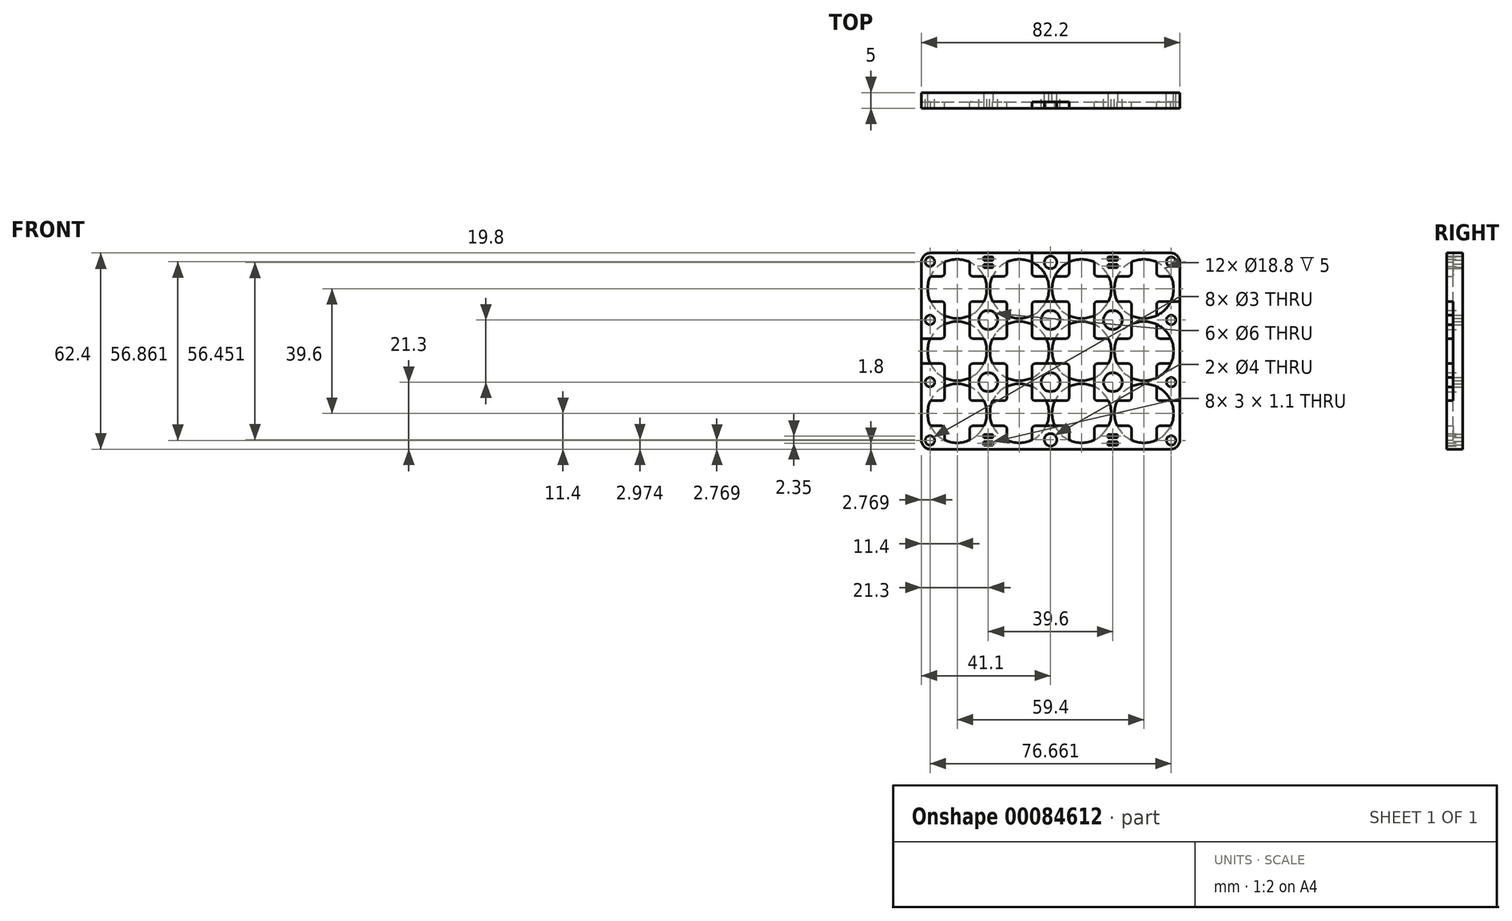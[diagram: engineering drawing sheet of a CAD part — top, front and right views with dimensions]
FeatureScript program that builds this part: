
annotation { "Feature Type Name" : "Feature", "Feature Type Description" : "" }
export const myFeature = defineFeature(function(context is Context, id is Id, definition is map)
    precondition{}
    {
        {
            var Q0;
            Q0=qCreatedBy(makeId("Front.planeOp"),FACE);
            var sketch = newSketch(context, id + "F0", { "sketchPlane" : qUnion([Q0]) });
            skCircle(sketch, "E0", {"center": v(0, 0) * mm, "radius": 9.4 * mm});
            skCircle(sketch, "E1.0.1.0", {"center": v(0, 19.8) * mm, "radius": 9.4 * mm});
            skCircle(sketch, "E1.0.2.0", {"center": v(0, 39.6) * mm, "radius": 9.4 * mm});
            skCircle(sketch, "E1.1.0.0", {"center": v(19.8, 0) * mm, "radius": 9.4 * mm});
            skCircle(sketch, "E1.1.1.0", {"center": v(19.8, 19.8) * mm, "radius": 9.4 * mm});
            skCircle(sketch, "E1.1.2.0", {"center": v(19.8, 39.6) * mm, "radius": 9.4 * mm});
            skCircle(sketch, "E1.2.0.0", {"center": v(39.6, 0) * mm, "radius": 9.4 * mm});
            skCircle(sketch, "E1.2.1.0", {"center": v(39.6, 19.8) * mm, "radius": 9.4 * mm});
            skCircle(sketch, "E1.2.2.0", {"center": v(39.6, 39.6) * mm, "radius": 9.4 * mm});
            skCircle(sketch, "E1.3.0.0", {"center": v(59.4, 0) * mm, "radius": 9.4 * mm});
            skCircle(sketch, "E1.3.1.0", {"center": v(59.4, 19.8) * mm, "radius": 9.4 * mm});
            skCircle(sketch, "E1.3.2.0", {"center": v(59.4, 39.6) * mm, "radius": 9.4 * mm});
            skLineSegment(sketch, "E1.direction1", {"start": v(0, 0) * mm, "end": v(19.8, 0) * mm, "construction": true});
            skLineSegment(sketch, "E1.direction2", {"start": v(0, 0) * mm, "end": v(0, 19.8) * mm, "construction": true});
            skLineSegment(sketch, "E2", {"start": v(-9.4, 19.8) * mm, "end": v(68.8, 19.8) * mm, "construction": true});
            skLineSegment(sketch, "E3", {"start": v(29.7, 19.8) * mm, "end": v(29.7, -16.3) * mm, "construction": true});
            skLineSegment(sketch, "E4.bottom", {"start": v(70.8, -11.4) * mm, "end": v(-11.4, -11.4) * mm});
            skLineSegment(sketch, "E4.top", {"start": v(70.8, 51) * mm, "end": v(-11.4, 51) * mm});
            skLineSegment(sketch, "E4.left", {"start": v(70.8, -11.4) * mm, "end": v(70.8, 51) * mm});
            skLineSegment(sketch, "E4.right", {"start": v(-11.4, -11.4) * mm, "end": v(-11.4, 51) * mm});
            skPoint(sketch, "E4.middle", {"position": v(29.7, 19.8) * mm});
            skLineSegment(sketch, "E5", {"start": v(19.8, 19.8) * mm, "end": v(0, 0) * mm, "construction": true});
            skLineSegment(sketch, "E6", {"start": v(19.8, 0) * mm, "end": v(0, 19.8) * mm, "construction": true});
            skCircle(sketch, "E7", {"center": v(9.9, 9.9) * mm, "radius": 3 * mm});
            skCircle(sketch, "E8.0.1.0", {"center": v(9.9, 29.7) * mm, "radius": 3 * mm});
            skCircle(sketch, "E8.1.0.0", {"center": v(29.7, 9.9) * mm, "radius": 3 * mm});
            skCircle(sketch, "E8.1.1.0", {"center": v(29.7, 29.7) * mm, "radius": 3 * mm});
            skCircle(sketch, "E8.2.0.0", {"center": v(49.5, 9.9) * mm, "radius": 3 * mm});
            skCircle(sketch, "E8.2.1.0", {"center": v(49.5, 29.7) * mm, "radius": 3 * mm});
            skLineSegment(sketch, "E8.direction1", {"start": v(9.9, 9.9) * mm, "end": v(29.7, 9.9) * mm, "construction": true});
            skLineSegment(sketch, "E8.direction2", {"start": v(9.9, 9.9) * mm, "end": v(9.9, 29.7) * mm, "construction": true});
            skLineSegment(sketch, "E9", {"start": v(9.9, 0) * mm, "end": v(9.9, -11.4) * mm, "construction": true});
            skCircle(sketch, "E10.1.0.0", {"center": v(29.7, -8.43) * mm, "radius": 2 * mm});
            skLineSegment(sketch, "E10.direction1", {"start": v(9.9, -8.43) * mm, "end": v(29.7, -8.43) * mm, "construction": true});
            skCircle(sketch, "E11.MirrorC", {"center": v(29.7, 48.03) * mm, "radius": 2 * mm});
            skLineSegment(sketch, "E12", {"start": v(0, 0) * mm, "end": v(-11.4, -11.4) * mm, "construction": true});
            skCircle(sketch, "E13", {"center": v(-8.63, -8.63) * mm, "radius": 1.5 * mm});
            skCircle(sketch, "E14", {"center": v(-8.63, 9.9) * mm, "radius": 1.5 * mm});
            skCircle(sketch, "E15", {"center": v(-8.63, 29.7) * mm, "radius": 1.5 * mm});
            skCircle(sketch, "E16.MirrorC", {"center": v(-8.63, 48.23) * mm, "radius": 1.5 * mm});
            skCircle(sketch, "E17.MirrorC", {"center": v(68.03, -8.63) * mm, "radius": 1.5 * mm});
            skCircle(sketch, "E18.MirrorC", {"center": v(68.03, 9.9) * mm, "radius": 1.5 * mm});
            skCircle(sketch, "E19.MirrorC", {"center": v(68.03, 29.7) * mm, "radius": 1.5 * mm});
            skCircle(sketch, "E20.MirrorC", {"center": v(68.03, 48.23) * mm, "radius": 1.5 * mm});
            skSolve(sketch);
        }
        {
            var Q0;
            Q0=qSketchRegion(id+"F0",true);
            extrude(context, id + "F1", {"entities" : qUnion([Q0]), "depth" : 3 * mm});
        }
        {
            var Q0;
            Q0=makeQuery(id+"F1.opExtrude","SWEPT_EDGE",EDGE,{"disambiguationData":[OSD([sQuery(id+"F0.wireOp",EDGE,"E4.top"),sQuery(id+"F0.wireOp",EDGE,"E4.left")])]});
            var Q1;
            Q1=makeQuery(id+"F1.opExtrude","SWEPT_EDGE",EDGE,{"disambiguationData":[OSD([sQuery(id+"F0.wireOp",EDGE,"E4.top"),sQuery(id+"F0.wireOp",EDGE,"E4.right")])]});
            var Q2;
            Q2=makeQuery(id+"F1.opExtrude","SWEPT_EDGE",EDGE,{"disambiguationData":[OSD([sQuery(id+"F0.wireOp",EDGE,"E4.bottom"),sQuery(id+"F0.wireOp",EDGE,"E4.right")])]});
            var Q3;
            Q3=makeQuery(id+"F1.opExtrude","SWEPT_EDGE",EDGE,{"disambiguationData":[OSD([sQuery(id+"F0.wireOp",EDGE,"E4.bottom"),sQuery(id+"F0.wireOp",EDGE,"E4.left")])]});
            fillet(context, id + "F2", {"entities" : qUnion([Q0, Q1, Q2, Q3]), "radius" : 3 * mm, "tangentPropagation" : true, "conicFillet" : false});
        }
        {
            var Q0;
            Q0=makeQuery(id+"F1.opExtrude","CAP_FACE",FACE,{"disambiguationData":[OSD([sQuery(id+"F0.wireOp",EDGE,"E0"),sQuery(id+"F0.wireOp",EDGE,"E1.0.1.0"),sQuery(id+"F0.wireOp",EDGE,"E1.0.2.0"),sQuery(id+"F0.wireOp",EDGE,"E1.1.0.0"),sQuery(id+"F0.wireOp",EDGE,"E1.1.1.0"),sQuery(id+"F0.wireOp",EDGE,"E1.1.2.0"),sQuery(id+"F0.wireOp",EDGE,"E1.2.0.0"),sQuery(id+"F0.wireOp",EDGE,"E1.2.1.0"),sQuery(id+"F0.wireOp",EDGE,"E1.2.2.0"),sQuery(id+"F0.wireOp",EDGE,"E1.3.0.0"),sQuery(id+"F0.wireOp",EDGE,"E1.3.1.0"),sQuery(id+"F0.wireOp",EDGE,"E1.3.2.0"),sQuery(id+"F0.wireOp",EDGE,"E4.bottom"),sQuery(id+"F0.wireOp",EDGE,"E4.top"),sQuery(id+"F0.wireOp",EDGE,"E4.left"),sQuery(id+"F0.wireOp",EDGE,"E4.right"),sQuery(id+"F0.wireOp",EDGE,"E7"),sQuery(id+"F0.wireOp",EDGE,"E8.0.1.0"),sQuery(id+"F0.wireOp",EDGE,"E8.1.0.0"),sQuery(id+"F0.wireOp",EDGE,"E8.1.1.0"),sQuery(id+"F0.wireOp",EDGE,"E8.2.0.0"),sQuery(id+"F0.wireOp",EDGE,"E8.2.1.0"),sQuery(id+"F0.wireOp",EDGE,"EQu0VpH5-7skk-RFPN-a941-U7lPeWaJFOTF"),sQuery(id+"F0.wireOp",EDGE,"E10.1.0.0"),sQuery(id+"F0.wireOp",EDGE,"E10.2.0.0"),sQuery(id+"F0.wireOp",EDGE,"d1583e0b-7ce3-4cbd-bf89-e67b3cb1275a0.MirrorC"),sQuery(id+"F0.wireOp",EDGE,"E11.MirrorC"),sQuery(id+"F0.wireOp",EDGE,"091dc890-a7a3-4dd7-b955-14caaaf945470.MirrorC"),sQuery(id+"F0.wireOp",EDGE,"E13"),sQuery(id+"F0.wireOp",EDGE,"E14"),sQuery(id+"F0.wireOp",EDGE,"E15"),sQuery(id+"F0.wireOp",EDGE,"E16.MirrorC"),sQuery(id+"F0.wireOp",EDGE,"E17.MirrorC"),sQuery(id+"F0.wireOp",EDGE,"E18.MirrorC"),sQuery(id+"F0.wireOp",EDGE,"E19.MirrorC"),sQuery(id+"F0.wireOp",EDGE,"E20.MirrorC")])],"isStart":false});
            var sketch = newSketch(context, id + "F3", { "sketchPlane" : qUnion([Q0]) });
            skLineSegment(sketch, "E21.0", {"start": v(67.8, 51) * mm, "end": v(-8.4, 51) * mm});
            skArc(sketch, "E21.1", {"start": v(-8.4, 51) * mm, "mid": v(-10.52, 50.12) * mm, "end": v(-11.4, 48) * mm});
            skLineSegment(sketch, "E21.2", {"start": v(-11.4, -8.4) * mm, "end": v(-11.4, 35.6) * mm});
            skArc(sketch, "E21.3", {"start": v(-11.4, -8.4) * mm, "mid": v(-10.52, -10.52) * mm, "end": v(-8.4, -11.4) * mm});
            skLineSegment(sketch, "E21.4", {"start": v(67.8, -11.4) * mm, "end": v(-8.4, -11.4) * mm});
            skArc(sketch, "E21.5", {"start": v(67.8, -11.4) * mm, "mid": v(69.92, -10.52) * mm, "end": v(70.8, -8.4) * mm});
            skLineSegment(sketch, "E21.6", {"start": v(70.8, -8.4) * mm, "end": v(70.8, 48) * mm});
            skArc(sketch, "E21.7", {"start": v(70.8, 48) * mm, "mid": v(69.92, 50.12) * mm, "end": v(67.8, 51) * mm});
            skCircle(sketch, "E21.8", {"center": v(59.4, 39.6) * mm, "radius": 9.4 * mm});
            skCircle(sketch, "E21.9", {"center": v(39.6, 39.6) * mm, "radius": 9.4 * mm});
            skCircle(sketch, "E21.10", {"center": v(19.8, 39.6) * mm, "radius": 9.4 * mm});
            skArc(sketch, "E21.11", {"start": v(-8.5, 43.6) * mm, "mid": v(-9.4, 39.6) * mm, "end": v(-8.5, 35.6) * mm});
            skCircle(sketch, "E21.12", {"center": v(0, 19.8) * mm, "radius": 9.4 * mm});
            skCircle(sketch, "E21.13", {"center": v(19.8, 19.8) * mm, "radius": 9.4 * mm});
            skCircle(sketch, "E21.14", {"center": v(39.6, 19.8) * mm, "radius": 9.4 * mm});
            skCircle(sketch, "E21.15", {"center": v(59.4, 19.8) * mm, "radius": 9.4 * mm});
            skCircle(sketch, "E21.16", {"center": v(59.4, 0) * mm, "radius": 9.4 * mm});
            skCircle(sketch, "E21.17", {"center": v(39.6, 0) * mm, "radius": 9.4 * mm});
            skCircle(sketch, "E21.18", {"center": v(19.8, 0) * mm, "radius": 9.4 * mm});
            skCircle(sketch, "E21.19", {"center": v(0, 0) * mm, "radius": 9.4 * mm});
            skLineSegment(sketch, "E22.left", {"start": v(-11.4, 39.6) * mm, "end": v(-11.4, 43.6) * mm});
            skLineSegment(sketch, "E22.right", {"start": v(70.8, 39.6) * mm, "end": v(70.8, 43.6) * mm});
            skLineSegment(sketch, "E23.trimOffspring", {"start": v(-11.4, 43.6) * mm, "end": v(-11.4, 48) * mm});
            skLineSegment(sketch, "E24", {"start": v(-4, 51) * mm, "end": v(-4, 43.6) * mm});
            skLineSegment(sketch, "E25.MirrorCS", {"start": v(4, 51) * mm, "end": v(4, 43.6) * mm});
            skLineSegment(sketch, "E26", {"start": v(-11.4, -4) * mm, "end": v(-4, -4) * mm});
            skLineSegment(sketch, "E27.MirrorCS", {"start": v(-11.4, 4) * mm, "end": v(-4, 4) * mm});
            skLineSegment(sketch, "E28.1.0.0", {"start": v(15.8, 51) * mm, "end": v(15.8, 43.6) * mm});
            skLineSegment(sketch, "E28.1.0.1", {"start": v(23.8, 51) * mm, "end": v(23.8, 43.6) * mm});
            skLineSegment(sketch, "E28.2.0.0", {"start": v(35.6, 51) * mm, "end": v(35.6, 43.6) * mm});
            skLineSegment(sketch, "E28.2.0.1", {"start": v(43.6, 51) * mm, "end": v(43.6, 43.6) * mm});
            skLineSegment(sketch, "E28.3.0.0", {"start": v(55.4, 51) * mm, "end": v(55.4, 43.6) * mm});
            skLineSegment(sketch, "E28.3.0.1", {"start": v(63.4, 51) * mm, "end": v(63.4, 43.6) * mm});
            skLineSegment(sketch, "E28.direction1", {"start": v(-4, -11.4) * mm, "end": v(15.8, -11.4) * mm, "construction": true});
            skLineSegment(sketch, "E29.0.1.0", {"start": v(-11.4, 23.8) * mm, "end": v(-4, 23.8) * mm});
            skLineSegment(sketch, "E29.0.1.1", {"start": v(-11.4, 15.8) * mm, "end": v(-4, 15.8) * mm});
            skLineSegment(sketch, "E29.0.2.0", {"start": v(-11.4, 43.6) * mm, "end": v(-4, 43.6) * mm});
            skLineSegment(sketch, "E29.0.2.1", {"start": v(-11.4, 35.6) * mm, "end": v(-4, 35.6) * mm});
            skLineSegment(sketch, "E29.direction1", {"start": v(-11.4, 4) * mm, "end": v(-4, 4) * mm, "construction": true});
            skLineSegment(sketch, "E29.direction2", {"start": v(-11.4, 4) * mm, "end": v(-11.4, 23.8) * mm, "construction": true});
            skLineSegment(sketch, "E30.trimOffspring", {"start": v(4, 35.6) * mm, "end": v(15.8, 35.6) * mm});
            skLineSegment(sketch, "E31.trimOffspring", {"start": v(4, 43.6) * mm, "end": v(15.8, 43.6) * mm});
            skLineSegment(sketch, "E32.trimOffspring", {"start": v(4, 35.6) * mm, "end": v(4, 23.8) * mm});
            skLineSegment(sketch, "E33.trimOffspring", {"start": v(-4, 35.6) * mm, "end": v(-4, 23.8) * mm});
            skLineSegment(sketch, "E34.trimOffspring", {"start": v(15.8, 35.6) * mm, "end": v(15.8, 23.8) * mm});
            skLineSegment(sketch, "E35.trimOffspring", {"start": v(23.8, 35.6) * mm, "end": v(23.8, 23.8) * mm});
            skLineSegment(sketch, "E36.trimOffspring", {"start": v(35.6, 35.6) * mm, "end": v(35.6, 23.8) * mm});
            skLineSegment(sketch, "E37.trimOffspring", {"start": v(43.6, 35.6) * mm, "end": v(43.6, 23.8) * mm});
            skLineSegment(sketch, "E38.trimOffspring", {"start": v(55.4, 35.6) * mm, "end": v(55.4, 23.8) * mm});
            skLineSegment(sketch, "E39.trimOffspring", {"start": v(63.4, 35.6) * mm, "end": v(63.4, 23.8) * mm});
            skLineSegment(sketch, "E40.trimOffspring", {"start": v(23.8, 43.6) * mm, "end": v(35.6, 43.6) * mm});
            skLineSegment(sketch, "E41.trimOffspring", {"start": v(43.6, 43.6) * mm, "end": v(55.4, 43.6) * mm});
            skLineSegment(sketch, "E42.trimOffspring", {"start": v(63.4, 43.6) * mm, "end": v(70.8, 43.6) * mm});
            skLineSegment(sketch, "E43.trimOffspring", {"start": v(63.4, 35.6) * mm, "end": v(70.8, 35.6) * mm});
            skLineSegment(sketch, "E44.trimOffspring", {"start": v(43.6, 35.6) * mm, "end": v(55.4, 35.6) * mm});
            skLineSegment(sketch, "E45.trimOffspring", {"start": v(23.8, 35.6) * mm, "end": v(35.6, 35.6) * mm});
            skLineSegment(sketch, "E46.trimOffspring", {"start": v(4, 23.8) * mm, "end": v(15.8, 23.8) * mm});
            skLineSegment(sketch, "E47.trimOffspring", {"start": v(4, 15.8) * mm, "end": v(11.3, 15.8) * mm});
            skLineSegment(sketch, "E48.trimOffspring", {"start": v(-4, 15.8) * mm, "end": v(-4, 4) * mm});
            skLineSegment(sketch, "E49.trimOffspring", {"start": v(4, 15.8) * mm, "end": v(4, 4) * mm});
            skLineSegment(sketch, "E50.trimOffspring", {"start": v(15.8, 15.8) * mm, "end": v(15.8, 4) * mm});
            skLineSegment(sketch, "E51.trimOffspring", {"start": v(23.8, 15.8) * mm, "end": v(23.8, 4) * mm});
            skLineSegment(sketch, "E52.trimOffspring", {"start": v(35.6, 15.8) * mm, "end": v(35.6, 4) * mm});
            skLineSegment(sketch, "E53.trimOffspring", {"start": v(43.6, 15.8) * mm, "end": v(43.6, 4) * mm});
            skLineSegment(sketch, "E54.trimOffspring", {"start": v(55.4, 15.8) * mm, "end": v(55.4, 4) * mm});
            skLineSegment(sketch, "E55.trimOffspring", {"start": v(63.4, 15.8) * mm, "end": v(63.4, 4) * mm});
            skLineSegment(sketch, "E56.trimOffspring", {"start": v(23.8, 23.8) * mm, "end": v(35.6, 23.8) * mm});
            skLineSegment(sketch, "E57.trimOffspring", {"start": v(43.6, 23.8) * mm, "end": v(55.4, 23.8) * mm});
            skLineSegment(sketch, "E58.trimOffspring", {"start": v(63.4, 23.8) * mm, "end": v(70.8, 23.8) * mm});
            skLineSegment(sketch, "E59.trimOffspring", {"start": v(23.8, 15.8) * mm, "end": v(35.6, 15.8) * mm});
            skLineSegment(sketch, "E60.trimOffspring", {"start": v(63.4, 15.8) * mm, "end": v(70.8, 15.8) * mm});
            skLineSegment(sketch, "E61.trimOffspring", {"start": v(63.4, 4) * mm, "end": v(70.8, 4) * mm});
            skLineSegment(sketch, "E62.trimOffspring", {"start": v(43.6, 4) * mm, "end": v(55.4, 4) * mm});
            skLineSegment(sketch, "E63.trimOffspring", {"start": v(23.8, 4) * mm, "end": v(35.6, 4) * mm});
            skLineSegment(sketch, "E64.trimOffspring", {"start": v(4, 4) * mm, "end": v(15.8, 4) * mm});
            skLineSegment(sketch, "E65.trimOffspring", {"start": v(4, -4) * mm, "end": v(11.3, -4) * mm});
            skLineSegment(sketch, "E66.trimOffspring", {"start": v(23.8, -4) * mm, "end": v(35.6, -4) * mm});
            skLineSegment(sketch, "E67.trimOffspring", {"start": v(63.4, -4) * mm, "end": v(70.8, -4) * mm});
            skLineSegment(sketch, "E68.trimOffspring", {"start": v(55.4, -4) * mm, "end": v(55.4, -11.4) * mm});
            skLineSegment(sketch, "E69.trimOffspring", {"start": v(63.4, -4) * mm, "end": v(63.4, -11.4) * mm});
            skLineSegment(sketch, "E70.trimOffspring", {"start": v(43.6, -4) * mm, "end": v(43.6, -11.4) * mm});
            skLineSegment(sketch, "E71.trimOffspring", {"start": v(35.6, -4) * mm, "end": v(35.6, -11.4) * mm});
            skLineSegment(sketch, "E72.trimOffspring", {"start": v(23.8, -4) * mm, "end": v(23.8, -11.4) * mm});
            skLineSegment(sketch, "E73.trimOffspring", {"start": v(4, -4) * mm, "end": v(4, -11.4) * mm});
            skLineSegment(sketch, "E74.trimOffspring", {"start": v(-4, -4) * mm, "end": v(-4, -11.4) * mm});
            skLineSegment(sketch, "E75", {"start": v(11.3, 15.8) * mm, "end": v(15.8, 15.8) * mm});
            skLineSegment(sketch, "E76", {"start": v(11.3, -4) * mm, "end": v(15.8, -4) * mm});
            skLineSegment(sketch, "E77.trimOffspring", {"start": v(15.8, -4) * mm, "end": v(15.8, -11.4) * mm});
            skLineSegment(sketch, "E78.trimOffspring", {"start": v(43.6, 15.8) * mm, "end": v(55.4, 15.8) * mm});
            skLineSegment(sketch, "E79.trimOffspring", {"start": v(4, 4) * mm, "end": v(13.6, 4) * mm, "construction": true});
            skLineSegment(sketch, "E80.trimOffspring", {"start": v(43.6, -4) * mm, "end": v(55.4, -4) * mm});
            skArc(sketch, "E81.trimOffspring", {"start": v(4, 48.1) * mm, "mid": v(0, 49) * mm, "end": v(-4, 48.1) * mm});
            skArc(sketch, "E82.trimOffspring", {"start": v(8.5, 35.6) * mm, "mid": v(9.4, 39.6) * mm, "end": v(8.5, 43.6) * mm});
            skArc(sketch, "E83.trimOffspring", {"start": v(-4, 31.1) * mm, "mid": v(0, 30.2) * mm, "end": v(4, 31.1) * mm});
            skSolve(sketch);
        }
        {
            var Q0;
            {var subQ6=sQuery(id+"F3.wireOp",EDGE,"E21.1");Q0=makeQuery(id+"F3.imprint","IMPRINT",FACE,{"disambiguationData":[TD([[makeQuery(id+"F3.imprint","IMPRINT",EDGE,{"derivedFrom":subQ6}),1.0]])]});}
            var Q1;
            {var subQ0=sQuery(id+"F3.wireOp",EDGE,"E29.0.2.0");var subQ1=sQuery(id+"F3.wireOp",EDGE,"E24");var subQ2=makeQuery(id+"F3.imprint","INTERSECT",VERTEX,{"derivedFrom":[subQ1,subQ0]});Q1=makeQuery(id+"F3.imprint","IMPRINT",FACE,{"disambiguationData":[TD([[makeQuery(id+"F3.imprint","IMPRINT",EDGE,{"disambiguationData":[TD([[subQ2,1.0]])],"derivedFrom":subQ1}),-1.0]])]});}
            var Q2;
            {var subQ0=sQuery(id+"F3.wireOp",EDGE,"E31.trimOffspring");var subQ1=sQuery(id+"F3.wireOp",EDGE,"E25.MirrorCS");var subQ2=makeQuery(id+"F3.imprint","INTERSECT",VERTEX,{"derivedFrom":[subQ1,subQ0]});Q2=makeQuery(id+"F3.imprint","IMPRINT",FACE,{"disambiguationData":[TD([[makeQuery(id+"F3.imprint","IMPRINT",EDGE,{"disambiguationData":[TD([[subQ2,1.0]])],"derivedFrom":subQ1}),1.0]])]});}
            var Q3;
            Q3=makeQuery(id+"F3.imprint","IMPRINT",FACE,{"disambiguationData":[TD([[makeQuery(id+"F3.imprint","IMPRINT",EDGE,{"derivedFrom":makeQuery(id+"F1.opExtrude","CAP_EDGE",EDGE,{"disambiguationData":[OSD([sQuery(id+"F0.wireOp",EDGE,"d1583e0b-7ce3-4cbd-bf89-e67b3cb1275a0.MirrorC")])],"isStart":false})}),1.0]])]});
            var Q4;
            {var subQ0=sQuery(id+"F3.wireOp",EDGE,"E31.trimOffspring");var subQ1=sQuery(id+"F3.wireOp",EDGE,"E28.1.0.0");var subQ2=makeQuery(id+"F3.imprint","INTERSECT",VERTEX,{"derivedFrom":[subQ1,subQ0]});Q4=makeQuery(id+"F3.imprint","IMPRINT",FACE,{"disambiguationData":[TD([[makeQuery(id+"F3.imprint","IMPRINT",EDGE,{"disambiguationData":[TD([[subQ2,1.0]])],"derivedFrom":subQ1}),-1.0]])]});}
            var Q5;
            {var subQ0=sQuery(id+"F3.wireOp",EDGE,"E40.trimOffspring");var subQ1=sQuery(id+"F3.wireOp",EDGE,"E28.1.0.1");var subQ2=makeQuery(id+"F3.imprint","INTERSECT",VERTEX,{"derivedFrom":[subQ1,subQ0]});Q5=makeQuery(id+"F3.imprint","IMPRINT",FACE,{"disambiguationData":[TD([[makeQuery(id+"F3.imprint","IMPRINT",EDGE,{"disambiguationData":[TD([[subQ2,1.0]])],"derivedFrom":subQ1}),1.0]])]});}
            var Q6;
            Q6=makeQuery(id+"F3.imprint","IMPRINT",FACE,{"disambiguationData":[TD([[makeQuery(id+"F3.imprint","IMPRINT",EDGE,{"derivedFrom":makeQuery(id+"F1.opExtrude","CAP_EDGE",EDGE,{"disambiguationData":[OSD([sQuery(id+"F0.wireOp",EDGE,"E11.MirrorC")])],"isStart":false})}),1.0]])]});
            var Q7;
            {var subQ0=sQuery(id+"F3.wireOp",EDGE,"E28.2.0.0");var subQ1=sQuery(id+"F3.wireOp",EDGE,"E21.9");var subQ2=makeQuery(id+"F3.imprint","INTERSECT",VERTEX,{"derivedFrom":[subQ1,subQ0]});Q7=makeQuery(id+"F3.imprint","IMPRINT",FACE,{"disambiguationData":[TD([[makeQuery(id+"F3.imprint","IMPRINT",EDGE,{"disambiguationData":[TD([[subQ2,-1.0]])],"derivedFrom":subQ1}),1.0]])]});}
            var Q8;
            {var subQ0=sQuery(id+"F3.wireOp",EDGE,"E28.2.0.1");var subQ1=sQuery(id+"F3.wireOp",EDGE,"E21.9");var subQ2=makeQuery(id+"F3.imprint","INTERSECT",VERTEX,{"derivedFrom":[subQ1,subQ0]});Q8=makeQuery(id+"F3.imprint","IMPRINT",FACE,{"disambiguationData":[TD([[makeQuery(id+"F3.imprint","IMPRINT",EDGE,{"disambiguationData":[TD([[subQ2,1.0]])],"derivedFrom":subQ1}),1.0]])]});}
            var Q9;
            Q9=makeQuery(id+"F3.imprint","IMPRINT",FACE,{"disambiguationData":[TD([[makeQuery(id+"F3.imprint","IMPRINT",EDGE,{"derivedFrom":makeQuery(id+"F1.opExtrude","CAP_EDGE",EDGE,{"disambiguationData":[OSD([sQuery(id+"F0.wireOp",EDGE,"091dc890-a7a3-4dd7-b955-14caaaf945470.MirrorC")])],"isStart":false})}),1.0]])]});
            var Q10;
            {var subQ0=sQuery(id+"F3.wireOp",EDGE,"E41.trimOffspring");var subQ1=sQuery(id+"F3.wireOp",EDGE,"E28.3.0.0");var subQ2=makeQuery(id+"F3.imprint","INTERSECT",VERTEX,{"derivedFrom":[subQ1,subQ0]});Q10=makeQuery(id+"F3.imprint","IMPRINT",FACE,{"disambiguationData":[TD([[makeQuery(id+"F3.imprint","IMPRINT",EDGE,{"disambiguationData":[TD([[subQ2,1.0]])],"derivedFrom":subQ1}),-1.0]])]});}
            var Q11;
            {var subQ0=sQuery(id+"F3.wireOp",EDGE,"E42.trimOffspring");var subQ1=sQuery(id+"F3.wireOp",EDGE,"E28.3.0.1");var subQ2=makeQuery(id+"F3.imprint","INTERSECT",VERTEX,{"derivedFrom":[subQ1,subQ0]});Q11=makeQuery(id+"F3.imprint","IMPRINT",FACE,{"disambiguationData":[TD([[makeQuery(id+"F3.imprint","IMPRINT",EDGE,{"disambiguationData":[TD([[subQ2,1.0]])],"derivedFrom":subQ1}),1.0]])]});}
            var Q12;
            {var subQ9=sQuery(id+"F3.wireOp",EDGE,"E21.7");Q12=makeQuery(id+"F3.imprint","IMPRINT",FACE,{"disambiguationData":[TD([[makeQuery(id+"F3.imprint","IMPRINT",EDGE,{"derivedFrom":subQ9}),1.0]])]});}
            var Q13;
            {var subQ0=sQuery(id+"F3.wireOp",EDGE,"E58.trimOffspring");var subQ1=sQuery(id+"F3.wireOp",EDGE,"E39.trimOffspring");var subQ2=makeQuery(id+"F3.imprint","INTERSECT",VERTEX,{"derivedFrom":[subQ1,subQ0]});Q13=makeQuery(id+"F3.imprint","IMPRINT",FACE,{"disambiguationData":[TD([[makeQuery(id+"F3.imprint","IMPRINT",EDGE,{"disambiguationData":[TD([[subQ2,1.0]])],"derivedFrom":subQ1}),1.0]])]});}
            var Q14;
            Q14=makeQuery(id+"F3.imprint","IMPRINT",FACE,{"disambiguationData":[TD([[makeQuery(id+"F3.imprint","IMPRINT",EDGE,{"derivedFrom":makeQuery(id+"F1.opExtrude","CAP_EDGE",EDGE,{"disambiguationData":[OSD([sQuery(id+"F0.wireOp",EDGE,"E19.MirrorC")])],"isStart":false})}),1.0]])]});
            var Q15;
            {var subQ0=sQuery(id+"F3.wireOp",EDGE,"E43.trimOffspring");var subQ1=sQuery(id+"F3.wireOp",EDGE,"E39.trimOffspring");var subQ2=makeQuery(id+"F3.imprint","INTERSECT",VERTEX,{"derivedFrom":[subQ1,subQ0]});Q15=makeQuery(id+"F3.imprint","IMPRINT",FACE,{"disambiguationData":[TD([[makeQuery(id+"F3.imprint","IMPRINT",EDGE,{"disambiguationData":[TD([[subQ2,-1.0]])],"derivedFrom":subQ1}),1.0]])]});}
            var Q16;
            {var subQ0=sQuery(id+"F3.wireOp",EDGE,"E57.trimOffspring");var subQ1=sQuery(id+"F3.wireOp",EDGE,"E38.trimOffspring");var subQ2=makeQuery(id+"F3.imprint","INTERSECT",VERTEX,{"derivedFrom":[subQ1,subQ0]});Q16=makeQuery(id+"F3.imprint","IMPRINT",FACE,{"disambiguationData":[TD([[makeQuery(id+"F3.imprint","IMPRINT",EDGE,{"disambiguationData":[TD([[subQ2,1.0]])],"derivedFrom":subQ1}),-1.0]])]});}
            var Q17;
            {var subQ0=sQuery(id+"F3.wireOp",EDGE,"E57.trimOffspring");var subQ1=sQuery(id+"F3.wireOp",EDGE,"E37.trimOffspring");var subQ2=makeQuery(id+"F3.imprint","INTERSECT",VERTEX,{"derivedFrom":[subQ1,subQ0]});Q17=makeQuery(id+"F3.imprint","IMPRINT",FACE,{"disambiguationData":[TD([[makeQuery(id+"F3.imprint","IMPRINT",EDGE,{"disambiguationData":[TD([[subQ2,1.0]])],"derivedFrom":subQ1}),1.0]])]});}
            var Q18;
            {var subQ0=sQuery(id+"F3.wireOp",EDGE,"E37.trimOffspring");var subQ1=sQuery(id+"F3.wireOp",EDGE,"E21.9");var subQ2=makeQuery(id+"F3.imprint","INTERSECT",VERTEX,{"derivedFrom":[subQ1,subQ0]});Q18=makeQuery(id+"F3.imprint","IMPRINT",FACE,{"disambiguationData":[TD([[makeQuery(id+"F3.imprint","IMPRINT",EDGE,{"disambiguationData":[TD([[subQ2,-1.0]])],"derivedFrom":subQ1}),1.0]])]});}
            var Q19;
            {var subQ0=sQuery(id+"F3.wireOp",EDGE,"E44.trimOffspring");var subQ1=sQuery(id+"F3.wireOp",EDGE,"E38.trimOffspring");var subQ2=makeQuery(id+"F3.imprint","INTERSECT",VERTEX,{"derivedFrom":[subQ1,subQ0]});Q19=makeQuery(id+"F3.imprint","IMPRINT",FACE,{"disambiguationData":[TD([[makeQuery(id+"F3.imprint","IMPRINT",EDGE,{"disambiguationData":[TD([[subQ2,-1.0]])],"derivedFrom":subQ1}),-1.0]])]});}
            var Q20;
            Q20=makeQuery(id+"F3.imprint","IMPRINT",FACE,{"disambiguationData":[TD([[makeQuery(id+"F3.imprint","IMPRINT",EDGE,{"derivedFrom":makeQuery(id+"F1.opExtrude","CAP_EDGE",EDGE,{"disambiguationData":[OSD([sQuery(id+"F0.wireOp",EDGE,"E8.2.1.0")])],"isStart":false})}),-1.0]])]});
            var Q21;
            {var subQ0=sQuery(id+"F3.wireOp",EDGE,"E45.trimOffspring");var subQ1=sQuery(id+"F3.wireOp",EDGE,"E35.trimOffspring");var subQ2=makeQuery(id+"F3.imprint","INTERSECT",VERTEX,{"derivedFrom":[subQ1,subQ0]});Q21=makeQuery(id+"F3.imprint","IMPRINT",FACE,{"disambiguationData":[TD([[makeQuery(id+"F3.imprint","IMPRINT",EDGE,{"disambiguationData":[TD([[subQ2,-1.0]])],"derivedFrom":subQ1}),1.0]])]});}
            var Q22;
            {var subQ0=sQuery(id+"F3.wireOp",EDGE,"E56.trimOffspring");var subQ1=sQuery(id+"F3.wireOp",EDGE,"E35.trimOffspring");var subQ2=makeQuery(id+"F3.imprint","INTERSECT",VERTEX,{"derivedFrom":[subQ1,subQ0]});Q22=makeQuery(id+"F3.imprint","IMPRINT",FACE,{"disambiguationData":[TD([[makeQuery(id+"F3.imprint","IMPRINT",EDGE,{"disambiguationData":[TD([[subQ2,1.0]])],"derivedFrom":subQ1}),1.0]])]});}
            var Q23;
            {var subQ0=sQuery(id+"F3.wireOp",EDGE,"E56.trimOffspring");var subQ1=sQuery(id+"F3.wireOp",EDGE,"E36.trimOffspring");var subQ2=makeQuery(id+"F3.imprint","INTERSECT",VERTEX,{"derivedFrom":[subQ1,subQ0]});Q23=makeQuery(id+"F3.imprint","IMPRINT",FACE,{"disambiguationData":[TD([[makeQuery(id+"F3.imprint","IMPRINT",EDGE,{"disambiguationData":[TD([[subQ2,1.0]])],"derivedFrom":subQ1}),-1.0]])]});}
            var Q24;
            {var subQ0=sQuery(id+"F3.wireOp",EDGE,"E45.trimOffspring");var subQ1=sQuery(id+"F3.wireOp",EDGE,"E21.9");var subQ2=makeQuery(id+"F3.imprint","INTERSECT",VERTEX,{"derivedFrom":[subQ1,subQ0]});Q24=makeQuery(id+"F3.imprint","IMPRINT",FACE,{"disambiguationData":[TD([[makeQuery(id+"F3.imprint","IMPRINT",EDGE,{"disambiguationData":[TD([[subQ2,-1.0]])],"derivedFrom":subQ1}),1.0]])]});}
            var Q25;
            Q25=makeQuery(id+"F3.imprint","IMPRINT",FACE,{"disambiguationData":[TD([[makeQuery(id+"F3.imprint","IMPRINT",EDGE,{"derivedFrom":makeQuery(id+"F1.opExtrude","CAP_EDGE",EDGE,{"disambiguationData":[OSD([sQuery(id+"F0.wireOp",EDGE,"E8.1.1.0")])],"isStart":false})}),-1.0]])]});
            var Q26;
            Q26=makeQuery(id+"F3.imprint","IMPRINT",FACE,{"disambiguationData":[TD([[makeQuery(id+"F3.imprint","IMPRINT",EDGE,{"derivedFrom":makeQuery(id+"F1.opExtrude","CAP_EDGE",EDGE,{"disambiguationData":[OSD([sQuery(id+"F0.wireOp",EDGE,"E8.0.1.0")])],"isStart":false})}),-1.0]])]});
            var Q27;
            {var subQ0=sQuery(id+"F3.wireOp",EDGE,"E32.trimOffspring");var subQ1=sQuery(id+"F3.wireOp",EDGE,"E30.trimOffspring");var subQ2=makeQuery(id+"F3.imprint","INTERSECT",VERTEX,{"derivedFrom":[subQ1,subQ0]});Q27=makeQuery(id+"F3.imprint","IMPRINT",FACE,{"disambiguationData":[TD([[makeQuery(id+"F3.imprint","IMPRINT",EDGE,{"disambiguationData":[TD([[subQ2,-1.0]])],"derivedFrom":subQ1}),-1.0]])]});}
            var Q28;
            {var subQ0=sQuery(id+"F3.wireOp",EDGE,"E34.trimOffspring");var subQ1=sQuery(id+"F3.wireOp",EDGE,"E30.trimOffspring");var subQ2=makeQuery(id+"F3.imprint","INTERSECT",VERTEX,{"derivedFrom":[subQ1,subQ0]});Q28=makeQuery(id+"F3.imprint","IMPRINT",FACE,{"disambiguationData":[TD([[makeQuery(id+"F3.imprint","IMPRINT",EDGE,{"disambiguationData":[TD([[subQ2,1.0]])],"derivedFrom":subQ1}),-1.0]])]});}
            var Q29;
            {var subQ0=sQuery(id+"F3.wireOp",EDGE,"E46.trimOffspring");var subQ1=sQuery(id+"F3.wireOp",EDGE,"E34.trimOffspring");var subQ2=makeQuery(id+"F3.imprint","INTERSECT",VERTEX,{"derivedFrom":[subQ1,subQ0]});Q29=makeQuery(id+"F3.imprint","IMPRINT",FACE,{"disambiguationData":[TD([[makeQuery(id+"F3.imprint","IMPRINT",EDGE,{"disambiguationData":[TD([[subQ2,1.0]])],"derivedFrom":subQ1}),-1.0]])]});}
            var Q30;
            {var subQ0=sQuery(id+"F3.wireOp",EDGE,"E46.trimOffspring");var subQ1=sQuery(id+"F3.wireOp",EDGE,"E32.trimOffspring");var subQ2=makeQuery(id+"F3.imprint","INTERSECT",VERTEX,{"derivedFrom":[subQ1,subQ0]});Q30=makeQuery(id+"F3.imprint","IMPRINT",FACE,{"disambiguationData":[TD([[makeQuery(id+"F3.imprint","IMPRINT",EDGE,{"disambiguationData":[TD([[subQ2,1.0]])],"derivedFrom":subQ1}),1.0]])]});}
            var Q31;
            Q31=makeQuery(id+"F3.imprint","IMPRINT",FACE,{"disambiguationData":[TD([[makeQuery(id+"F3.imprint","IMPRINT",EDGE,{"derivedFrom":makeQuery(id+"F1.opExtrude","CAP_EDGE",EDGE,{"disambiguationData":[OSD([sQuery(id+"F0.wireOp",EDGE,"E14")])],"isStart":false})}),-1.0]])]});
            var Q32;
            {var subQ0=sQuery(id+"F3.wireOp",EDGE,"E48.trimOffspring");var subQ1=sQuery(id+"F3.wireOp",EDGE,"E29.0.1.1");var subQ2=makeQuery(id+"F3.imprint","INTERSECT",VERTEX,{"derivedFrom":[subQ1,subQ0]});Q32=makeQuery(id+"F3.imprint","IMPRINT",FACE,{"disambiguationData":[TD([[makeQuery(id+"F3.imprint","IMPRINT",EDGE,{"disambiguationData":[TD([[subQ2,1.0]])],"derivedFrom":subQ1}),-1.0]])]});}
            var Q33;
            {var subQ0=sQuery(id+"F3.wireOp",EDGE,"E48.trimOffspring");var subQ1=sQuery(id+"F3.wireOp",EDGE,"E27.MirrorCS");var subQ2=makeQuery(id+"F3.imprint","INTERSECT",VERTEX,{"derivedFrom":[subQ1,subQ0]});Q33=makeQuery(id+"F3.imprint","IMPRINT",FACE,{"disambiguationData":[TD([[makeQuery(id+"F3.imprint","IMPRINT",EDGE,{"disambiguationData":[TD([[subQ2,1.0]])],"derivedFrom":subQ1}),1.0]])]});}
            var Q34;
            {var subQ1=sQuery(id+"F3.wireOp",EDGE,"E21.3");Q34=makeQuery(id+"F3.imprint","IMPRINT",FACE,{"disambiguationData":[TD([[makeQuery(id+"F3.imprint","IMPRINT",EDGE,{"derivedFrom":subQ1}),1.0]])]});}
            var Q35;
            {var subQ0=sQuery(id+"F3.wireOp",EDGE,"E74.trimOffspring");var subQ1=sQuery(id+"F3.wireOp",EDGE,"E26");var subQ2=makeQuery(id+"F3.imprint","INTERSECT",VERTEX,{"derivedFrom":[subQ1,subQ0]});Q35=makeQuery(id+"F3.imprint","IMPRINT",FACE,{"disambiguationData":[TD([[makeQuery(id+"F3.imprint","IMPRINT",EDGE,{"disambiguationData":[TD([[subQ2,1.0]])],"derivedFrom":subQ1}),-1.0]])]});}
            var Q36;
            Q36=makeQuery(id+"F3.imprint","IMPRINT",FACE,{"disambiguationData":[TD([[makeQuery(id+"F3.imprint","IMPRINT",EDGE,{"derivedFrom":makeQuery(id+"F1.opExtrude","CAP_EDGE",EDGE,{"disambiguationData":[OSD([sQuery(id+"F0.wireOp",EDGE,"EQu0VpH5-7skk-RFPN-a941-U7lPeWaJFOTF")])],"isStart":false})}),-1.0]])]});
            var Q37;
            {var subQ0=sQuery(id+"F3.wireOp",EDGE,"E73.trimOffspring");var subQ1=sQuery(id+"F3.wireOp",EDGE,"E65.trimOffspring");var subQ2=makeQuery(id+"F3.imprint","INTERSECT",VERTEX,{"derivedFrom":[subQ1,subQ0]});Q37=makeQuery(id+"F3.imprint","IMPRINT",FACE,{"disambiguationData":[TD([[makeQuery(id+"F3.imprint","IMPRINT",EDGE,{"disambiguationData":[TD([[subQ2,-1.0]])],"derivedFrom":subQ1}),-1.0]])]});}
            var Q38;
            {var subQ0=sQuery(id+"F3.wireOp",EDGE,"E76");Q38=makeQuery(id+"F3.imprint","IMPRINT",FACE,{"disambiguationData":[TD([[makeQuery(id+"F3.imprint","IMPRINT",EDGE,{"derivedFrom":subQ0}),-1.0]])]});}
            var Q39;
            Q39=makeQuery(id+"F3.imprint","IMPRINT",FACE,{"disambiguationData":[TD([[makeQuery(id+"F3.imprint","IMPRINT",EDGE,{"derivedFrom":makeQuery(id+"F1.opExtrude","CAP_EDGE",EDGE,{"disambiguationData":[OSD([sQuery(id+"F0.wireOp",EDGE,"E10.1.0.0")])],"isStart":false})}),-1.0]])]});
            var Q40;
            {var subQ0=sQuery(id+"F3.wireOp",EDGE,"E72.trimOffspring");var subQ1=sQuery(id+"F3.wireOp",EDGE,"E66.trimOffspring");var subQ2=makeQuery(id+"F3.imprint","INTERSECT",VERTEX,{"derivedFrom":[subQ1,subQ0]});Q40=makeQuery(id+"F3.imprint","IMPRINT",FACE,{"disambiguationData":[TD([[makeQuery(id+"F3.imprint","IMPRINT",EDGE,{"disambiguationData":[TD([[subQ2,-1.0]])],"derivedFrom":subQ1}),-1.0]])]});}
            var Q41;
            {var subQ0=sQuery(id+"F3.wireOp",EDGE,"E71.trimOffspring");var subQ1=sQuery(id+"F3.wireOp",EDGE,"E66.trimOffspring");var subQ2=makeQuery(id+"F3.imprint","INTERSECT",VERTEX,{"derivedFrom":[subQ1,subQ0]});Q41=makeQuery(id+"F3.imprint","IMPRINT",FACE,{"disambiguationData":[TD([[makeQuery(id+"F3.imprint","IMPRINT",EDGE,{"disambiguationData":[TD([[subQ2,1.0]])],"derivedFrom":subQ1}),-1.0]])]});}
            var Q42;
            Q42=makeQuery(id+"F3.imprint","IMPRINT",FACE,{"disambiguationData":[TD([[makeQuery(id+"F3.imprint","IMPRINT",EDGE,{"derivedFrom":makeQuery(id+"F1.opExtrude","CAP_EDGE",EDGE,{"disambiguationData":[OSD([sQuery(id+"F0.wireOp",EDGE,"E10.2.0.0")])],"isStart":false})}),-1.0]])]});
            var Q43;
            {var subQ0=sQuery(id+"F3.wireOp",EDGE,"E80.trimOffspring");var subQ1=sQuery(id+"F3.wireOp",EDGE,"E70.trimOffspring");var subQ2=makeQuery(id+"F3.imprint","INTERSECT",VERTEX,{"derivedFrom":[subQ1,subQ0]});Q43=makeQuery(id+"F3.imprint","IMPRINT",FACE,{"disambiguationData":[TD([[makeQuery(id+"F3.imprint","IMPRINT",EDGE,{"disambiguationData":[TD([[subQ2,-1.0]])],"derivedFrom":subQ1}),1.0]])]});}
            var Q44;
            {var subQ0=sQuery(id+"F3.wireOp",EDGE,"E80.trimOffspring");var subQ1=sQuery(id+"F3.wireOp",EDGE,"E68.trimOffspring");var subQ2=makeQuery(id+"F3.imprint","INTERSECT",VERTEX,{"derivedFrom":[subQ1,subQ0]});Q44=makeQuery(id+"F3.imprint","IMPRINT",FACE,{"disambiguationData":[TD([[makeQuery(id+"F3.imprint","IMPRINT",EDGE,{"disambiguationData":[TD([[subQ2,-1.0]])],"derivedFrom":subQ1}),-1.0]])]});}
            var Q45;
            {var subQ0=sQuery(id+"F3.wireOp",EDGE,"E69.trimOffspring");var subQ1=sQuery(id+"F3.wireOp",EDGE,"E67.trimOffspring");var subQ2=makeQuery(id+"F3.imprint","INTERSECT",VERTEX,{"derivedFrom":[subQ1,subQ0]});Q45=makeQuery(id+"F3.imprint","IMPRINT",FACE,{"disambiguationData":[TD([[makeQuery(id+"F3.imprint","IMPRINT",EDGE,{"disambiguationData":[TD([[subQ2,-1.0]])],"derivedFrom":subQ1}),-1.0]])]});}
            var Q46;
            {var subQ1=sQuery(id+"F3.wireOp",EDGE,"E21.5");Q46=makeQuery(id+"F3.imprint","IMPRINT",FACE,{"disambiguationData":[TD([[makeQuery(id+"F3.imprint","IMPRINT",EDGE,{"derivedFrom":subQ1}),1.0]])]});}
            var Q47;
            Q47=makeQuery(id+"F3.imprint","IMPRINT",FACE,{"disambiguationData":[TD([[makeQuery(id+"F3.imprint","IMPRINT",EDGE,{"derivedFrom":makeQuery(id+"F1.opExtrude","CAP_EDGE",EDGE,{"disambiguationData":[OSD([sQuery(id+"F0.wireOp",EDGE,"E18.MirrorC")])],"isStart":false})}),1.0]])]});
            var Q48;
            {var subQ0=sQuery(id+"F3.wireOp",EDGE,"E61.trimOffspring");var subQ1=sQuery(id+"F3.wireOp",EDGE,"E55.trimOffspring");var subQ2=makeQuery(id+"F3.imprint","INTERSECT",VERTEX,{"derivedFrom":[subQ1,subQ0]});Q48=makeQuery(id+"F3.imprint","IMPRINT",FACE,{"disambiguationData":[TD([[makeQuery(id+"F3.imprint","IMPRINT",EDGE,{"disambiguationData":[TD([[subQ2,1.0]])],"derivedFrom":subQ1}),1.0]])]});}
            var Q49;
            {var subQ0=sQuery(id+"F3.wireOp",EDGE,"E60.trimOffspring");var subQ1=sQuery(id+"F3.wireOp",EDGE,"E55.trimOffspring");var subQ2=makeQuery(id+"F3.imprint","INTERSECT",VERTEX,{"derivedFrom":[subQ1,subQ0]});Q49=makeQuery(id+"F3.imprint","IMPRINT",FACE,{"disambiguationData":[TD([[makeQuery(id+"F3.imprint","IMPRINT",EDGE,{"disambiguationData":[TD([[subQ2,-1.0]])],"derivedFrom":subQ1}),1.0]])]});}
            var Q50;
            {var subQ0=sQuery(id+"F3.wireOp",EDGE,"E62.trimOffspring");var subQ1=sQuery(id+"F3.wireOp",EDGE,"E54.trimOffspring");var subQ2=makeQuery(id+"F3.imprint","INTERSECT",VERTEX,{"derivedFrom":[subQ1,subQ0]});Q50=makeQuery(id+"F3.imprint","IMPRINT",FACE,{"disambiguationData":[TD([[makeQuery(id+"F3.imprint","IMPRINT",EDGE,{"disambiguationData":[TD([[subQ2,1.0]])],"derivedFrom":subQ1}),-1.0]])]});}
            var Q51;
            {var subQ0=sQuery(id+"F3.wireOp",EDGE,"E62.trimOffspring");var subQ1=sQuery(id+"F3.wireOp",EDGE,"E53.trimOffspring");var subQ2=makeQuery(id+"F3.imprint","INTERSECT",VERTEX,{"derivedFrom":[subQ1,subQ0]});Q51=makeQuery(id+"F3.imprint","IMPRINT",FACE,{"disambiguationData":[TD([[makeQuery(id+"F3.imprint","IMPRINT",EDGE,{"disambiguationData":[TD([[subQ2,1.0]])],"derivedFrom":subQ1}),1.0]])]});}
            var Q52;
            Q52=makeQuery(id+"F3.imprint","IMPRINT",FACE,{"disambiguationData":[TD([[makeQuery(id+"F3.imprint","IMPRINT",EDGE,{"derivedFrom":makeQuery(id+"F1.opExtrude","CAP_EDGE",EDGE,{"disambiguationData":[OSD([sQuery(id+"F0.wireOp",EDGE,"E8.2.0.0")])],"isStart":false})}),-1.0]])]});
            var Q53;
            {var subQ0=sQuery(id+"F3.wireOp",EDGE,"E78.trimOffspring");var subQ1=sQuery(id+"F3.wireOp",EDGE,"E53.trimOffspring");var subQ2=makeQuery(id+"F3.imprint","INTERSECT",VERTEX,{"derivedFrom":[subQ1,subQ0]});Q53=makeQuery(id+"F3.imprint","IMPRINT",FACE,{"disambiguationData":[TD([[makeQuery(id+"F3.imprint","IMPRINT",EDGE,{"disambiguationData":[TD([[subQ2,-1.0]])],"derivedFrom":subQ1}),1.0]])]});}
            var Q54;
            {var subQ0=sQuery(id+"F3.wireOp",EDGE,"E78.trimOffspring");var subQ1=sQuery(id+"F3.wireOp",EDGE,"E54.trimOffspring");var subQ2=makeQuery(id+"F3.imprint","INTERSECT",VERTEX,{"derivedFrom":[subQ1,subQ0]});Q54=makeQuery(id+"F3.imprint","IMPRINT",FACE,{"disambiguationData":[TD([[makeQuery(id+"F3.imprint","IMPRINT",EDGE,{"disambiguationData":[TD([[subQ2,-1.0]])],"derivedFrom":subQ1}),-1.0]])]});}
            var Q55;
            {var subQ0=sQuery(id+"F3.wireOp",EDGE,"E63.trimOffspring");var subQ1=sQuery(id+"F3.wireOp",EDGE,"E52.trimOffspring");var subQ2=makeQuery(id+"F3.imprint","INTERSECT",VERTEX,{"derivedFrom":[subQ1,subQ0]});Q55=makeQuery(id+"F3.imprint","IMPRINT",FACE,{"disambiguationData":[TD([[makeQuery(id+"F3.imprint","IMPRINT",EDGE,{"disambiguationData":[TD([[subQ2,1.0]])],"derivedFrom":subQ1}),-1.0]])]});}
            var Q56;
            {var subQ0=sQuery(id+"F3.wireOp",EDGE,"E63.trimOffspring");var subQ1=sQuery(id+"F3.wireOp",EDGE,"E51.trimOffspring");var subQ2=makeQuery(id+"F3.imprint","INTERSECT",VERTEX,{"derivedFrom":[subQ1,subQ0]});Q56=makeQuery(id+"F3.imprint","IMPRINT",FACE,{"disambiguationData":[TD([[makeQuery(id+"F3.imprint","IMPRINT",EDGE,{"disambiguationData":[TD([[subQ2,1.0]])],"derivedFrom":subQ1}),1.0]])]});}
            var Q57;
            {var subQ0=sQuery(id+"F3.wireOp",EDGE,"E59.trimOffspring");var subQ1=sQuery(id+"F3.wireOp",EDGE,"E51.trimOffspring");var subQ2=makeQuery(id+"F3.imprint","INTERSECT",VERTEX,{"derivedFrom":[subQ1,subQ0]});Q57=makeQuery(id+"F3.imprint","IMPRINT",FACE,{"disambiguationData":[TD([[makeQuery(id+"F3.imprint","IMPRINT",EDGE,{"disambiguationData":[TD([[subQ2,-1.0]])],"derivedFrom":subQ1}),1.0]])]});}
            var Q58;
            {var subQ0=sQuery(id+"F3.wireOp",EDGE,"E59.trimOffspring");var subQ1=sQuery(id+"F3.wireOp",EDGE,"E52.trimOffspring");var subQ2=makeQuery(id+"F3.imprint","INTERSECT",VERTEX,{"derivedFrom":[subQ1,subQ0]});Q58=makeQuery(id+"F3.imprint","IMPRINT",FACE,{"disambiguationData":[TD([[makeQuery(id+"F3.imprint","IMPRINT",EDGE,{"disambiguationData":[TD([[subQ2,-1.0]])],"derivedFrom":subQ1}),-1.0]])]});}
            var Q59;
            Q59=makeQuery(id+"F3.imprint","IMPRINT",FACE,{"disambiguationData":[TD([[makeQuery(id+"F3.imprint","IMPRINT",EDGE,{"derivedFrom":makeQuery(id+"F1.opExtrude","CAP_EDGE",EDGE,{"disambiguationData":[OSD([sQuery(id+"F0.wireOp",EDGE,"E8.1.0.0")])],"isStart":false})}),-1.0]])]});
            var Q60;
            Q60=makeQuery(id+"F3.imprint","IMPRINT",FACE,{"disambiguationData":[TD([[makeQuery(id+"F3.imprint","IMPRINT",EDGE,{"derivedFrom":makeQuery(id+"F1.opExtrude","CAP_EDGE",EDGE,{"disambiguationData":[OSD([sQuery(id+"F0.wireOp",EDGE,"E7")])],"isStart":false})}),-1.0]])]});
            var Q61;
            {var subQ0=sQuery(id+"F3.wireOp",EDGE,"E49.trimOffspring");var subQ1=sQuery(id+"F3.wireOp",EDGE,"E47.trimOffspring");var subQ2=makeQuery(id+"F3.imprint","INTERSECT",VERTEX,{"derivedFrom":[subQ1,subQ0]});Q61=makeQuery(id+"F3.imprint","IMPRINT",FACE,{"disambiguationData":[TD([[makeQuery(id+"F3.imprint","IMPRINT",EDGE,{"disambiguationData":[TD([[subQ2,-1.0]])],"derivedFrom":subQ1}),-1.0]])]});}
            var Q62;
            {var subQ0=sQuery(id+"F3.wireOp",EDGE,"E75");Q62=makeQuery(id+"F3.imprint","IMPRINT",FACE,{"disambiguationData":[TD([[makeQuery(id+"F3.imprint","IMPRINT",EDGE,{"derivedFrom":subQ0}),-1.0]])]});}
            var Q63;
            {var subQ0=sQuery(id+"F3.wireOp",EDGE,"E64.trimOffspring");var subQ1=sQuery(id+"F3.wireOp",EDGE,"E50.trimOffspring");var subQ2=makeQuery(id+"F3.imprint","INTERSECT",VERTEX,{"derivedFrom":[subQ1,subQ0]});Q63=makeQuery(id+"F3.imprint","IMPRINT",FACE,{"disambiguationData":[TD([[makeQuery(id+"F3.imprint","IMPRINT",EDGE,{"disambiguationData":[TD([[subQ2,1.0]])],"derivedFrom":subQ1}),-1.0]])]});}
            var Q64;
            {var subQ0=sQuery(id+"F3.wireOp",EDGE,"E64.trimOffspring");var subQ1=sQuery(id+"F3.wireOp",EDGE,"E49.trimOffspring");var subQ2=makeQuery(id+"F3.imprint","INTERSECT",VERTEX,{"derivedFrom":[subQ1,subQ0]});Q64=makeQuery(id+"F3.imprint","IMPRINT",FACE,{"disambiguationData":[TD([[makeQuery(id+"F3.imprint","IMPRINT",EDGE,{"disambiguationData":[TD([[subQ2,1.0]])],"derivedFrom":subQ1}),1.0]])]});}
            var Q65;
            Q65=makeQuery(id+"F3.imprint","IMPRINT",FACE,{"disambiguationData":[TD([[makeQuery(id+"F3.imprint","IMPRINT",EDGE,{"derivedFrom":makeQuery(id+"F1.opExtrude","CAP_EDGE",EDGE,{"disambiguationData":[OSD([sQuery(id+"F0.wireOp",EDGE,"E15")])],"isStart":false})}),-1.0]])]});
            var Q66;
            {var subQ0=sQuery(id+"F3.wireOp",EDGE,"E33.trimOffspring");var subQ1=sQuery(id+"F3.wireOp",EDGE,"E29.0.2.1");var subQ2=makeQuery(id+"F3.imprint","INTERSECT",VERTEX,{"derivedFrom":[subQ1,subQ0]});Q66=makeQuery(id+"F3.imprint","IMPRINT",FACE,{"disambiguationData":[TD([[makeQuery(id+"F3.imprint","IMPRINT",EDGE,{"disambiguationData":[TD([[subQ2,1.0]])],"derivedFrom":subQ1}),-1.0]])]});}
            var Q67;
            {var subQ0=sQuery(id+"F3.wireOp",EDGE,"E33.trimOffspring");var subQ1=sQuery(id+"F3.wireOp",EDGE,"E29.0.1.0");var subQ2=makeQuery(id+"F3.imprint","INTERSECT",VERTEX,{"derivedFrom":[subQ1,subQ0]});Q67=makeQuery(id+"F3.imprint","IMPRINT",FACE,{"disambiguationData":[TD([[makeQuery(id+"F3.imprint","IMPRINT",EDGE,{"disambiguationData":[TD([[subQ2,1.0]])],"derivedFrom":subQ1}),1.0]])]});}
            var Q68;
            {var subQ0=sQuery(id+"F3.wireOp",EDGE,"E28.1.0.0");var subQ1=sQuery(id+"F3.wireOp",EDGE,"E21.0");var subQ2=makeQuery(id+"F3.imprint","INTERSECT",VERTEX,{"derivedFrom":[subQ1,subQ0]});Q68=makeQuery(id+"F3.imprint","IMPRINT",FACE,{"disambiguationData":[TD([[makeQuery(id+"F3.imprint","IMPRINT",EDGE,{"disambiguationData":[TD([[subQ2,1.0]])],"derivedFrom":subQ1}),1.0]])]});}
            var Q69;
            {var subQ3=sQuery(id+"F3.wireOp",EDGE,"E21.11");Q69=makeQuery(id+"F3.imprint","IMPRINT",FACE,{"disambiguationData":[TD([[makeQuery(id+"F3.imprint","IMPRINT",EDGE,{"derivedFrom":subQ3}),-1.0]])]});}
            var Q70;
            {var subQ0=sQuery(id+"F3.wireOp",EDGE,"E26");var subQ1=sQuery(id+"F3.wireOp",EDGE,"E21.2");var subQ2=makeQuery(id+"F3.imprint","INTERSECT",VERTEX,{"derivedFrom":[subQ1,subQ0]});Q70=makeQuery(id+"F3.imprint","IMPRINT",FACE,{"disambiguationData":[TD([[makeQuery(id+"F3.imprint","IMPRINT",EDGE,{"disambiguationData":[TD([[subQ2,-1.0]])],"derivedFrom":subQ1}),-1.0]])]});}
            var Q71;
            {var subQ0=sQuery(id+"F3.wireOp",EDGE,"E28.2.0.0");var subQ1=sQuery(id+"F3.wireOp",EDGE,"E21.0");var subQ2=makeQuery(id+"F3.imprint","INTERSECT",VERTEX,{"derivedFrom":[subQ1,subQ0]});Q71=makeQuery(id+"F3.imprint","IMPRINT",FACE,{"disambiguationData":[TD([[makeQuery(id+"F3.imprint","IMPRINT",EDGE,{"disambiguationData":[TD([[subQ2,1.0]])],"derivedFrom":subQ1}),1.0]])]});}
            var Q72;
            {var subQ0=sQuery(id+"F3.wireOp",EDGE,"E22.right");Q72=makeQuery(id+"F3.imprint","IMPRINT",FACE,{"disambiguationData":[TD([[makeQuery(id+"F3.imprint","IMPRINT",EDGE,{"derivedFrom":subQ0}),1.0]])]});}
            var Q73;
            {var subQ0=sQuery(id+"F3.wireOp",EDGE,"E61.trimOffspring");var subQ1=sQuery(id+"F3.wireOp",EDGE,"E21.6");var subQ2=makeQuery(id+"F3.imprint","INTERSECT",VERTEX,{"derivedFrom":[subQ1,subQ0]});Q73=makeQuery(id+"F3.imprint","IMPRINT",FACE,{"disambiguationData":[TD([[makeQuery(id+"F3.imprint","IMPRINT",EDGE,{"disambiguationData":[TD([[subQ2,1.0]])],"derivedFrom":subQ1}),1.0]])]});}
            var Q74;
            {var subQ0=sQuery(id+"F3.wireOp",EDGE,"E68.trimOffspring");var subQ1=sQuery(id+"F3.wireOp",EDGE,"E21.4");var subQ2=makeQuery(id+"F3.imprint","INTERSECT",VERTEX,{"derivedFrom":[subQ1,subQ0]});Q74=makeQuery(id+"F3.imprint","IMPRINT",FACE,{"disambiguationData":[TD([[makeQuery(id+"F3.imprint","IMPRINT",EDGE,{"disambiguationData":[TD([[subQ2,1.0]])],"derivedFrom":subQ1}),-1.0]])]});}
            var Q75;
            {var subQ0=sQuery(id+"F3.wireOp",EDGE,"E70.trimOffspring");var subQ1=sQuery(id+"F3.wireOp",EDGE,"E21.4");var subQ2=makeQuery(id+"F3.imprint","INTERSECT",VERTEX,{"derivedFrom":[subQ1,subQ0]});Q75=makeQuery(id+"F3.imprint","IMPRINT",FACE,{"disambiguationData":[TD([[makeQuery(id+"F3.imprint","IMPRINT",EDGE,{"disambiguationData":[TD([[subQ2,-1.0]])],"derivedFrom":subQ1}),-1.0]])]});}
            var Q76;
            {var subQ0=sQuery(id+"F3.wireOp",EDGE,"E72.trimOffspring");var subQ1=sQuery(id+"F3.wireOp",EDGE,"E21.4");var subQ2=makeQuery(id+"F3.imprint","INTERSECT",VERTEX,{"derivedFrom":[subQ1,subQ0]});Q76=makeQuery(id+"F3.imprint","IMPRINT",FACE,{"disambiguationData":[TD([[makeQuery(id+"F3.imprint","IMPRINT",EDGE,{"disambiguationData":[TD([[subQ2,-1.0]])],"derivedFrom":subQ1}),-1.0]])]});}
            var Q77;
            {var subQ0=sQuery(id+"F3.wireOp",EDGE,"E73.trimOffspring");var subQ1=sQuery(id+"F3.wireOp",EDGE,"E21.4");var subQ2=makeQuery(id+"F3.imprint","INTERSECT",VERTEX,{"derivedFrom":[subQ1,subQ0]});Q77=makeQuery(id+"F3.imprint","IMPRINT",FACE,{"disambiguationData":[TD([[makeQuery(id+"F3.imprint","IMPRINT",EDGE,{"disambiguationData":[TD([[subQ2,-1.0]])],"derivedFrom":subQ1}),-1.0]])]});}
            var Q78;
            {var subQ5=sQuery(id+"F3.wireOp",EDGE,"E82.trimOffspring");Q78=makeQuery(id+"F3.imprint","IMPRINT",FACE,{"disambiguationData":[TD([[makeQuery(id+"F3.imprint","IMPRINT",EDGE,{"derivedFrom":subQ5}),-1.0]])]});}
            var Q79;
            {var subQ0=sQuery(id+"F3.wireOp",EDGE,"E46.trimOffspring");var subQ1=sQuery(id+"F3.wireOp",EDGE,"E21.12");var subQ2=makeQuery(id+"F3.imprint","INTERSECT",VERTEX,{"derivedFrom":[subQ1,subQ0]});Q79=makeQuery(id+"F3.imprint","IMPRINT",FACE,{"disambiguationData":[TD([[makeQuery(id+"F3.imprint","IMPRINT",EDGE,{"disambiguationData":[TD([[subQ2,1.0]])],"derivedFrom":subQ1}),-1.0]])]});}
            var Q80;
            {var subQ3=sQuery(id+"F3.wireOp",EDGE,"E64.trimOffspring");var subQ5=sQuery(id+"F3.wireOp",EDGE,"E21.19");var subQ6=makeQuery(id+"F3.imprint","INTERSECT",VERTEX,{"derivedFrom":[subQ5,subQ3]});Q80=makeQuery(id+"F3.imprint","IMPRINT",FACE,{"disambiguationData":[TD([[makeQuery(id+"F3.imprint","IMPRINT",EDGE,{"disambiguationData":[TD([[subQ6,1.0]])],"derivedFrom":subQ5}),-1.0]])]});}
            var Q81;
            {var subQ0=sQuery(id+"F3.wireOp",EDGE,"E62.trimOffspring");var subQ1=sQuery(id+"F3.wireOp",EDGE,"E21.16");var subQ2=makeQuery(id+"F3.imprint","INTERSECT",VERTEX,{"derivedFrom":[subQ1,subQ0]});Q81=makeQuery(id+"F3.imprint","IMPRINT",FACE,{"disambiguationData":[TD([[makeQuery(id+"F3.imprint","IMPRINT",EDGE,{"disambiguationData":[TD([[subQ2,-1.0]])],"derivedFrom":subQ1}),-1.0]])]});}
            var Q82;
            {var subQ0=sQuery(id+"F3.wireOp",EDGE,"E57.trimOffspring");var subQ1=sQuery(id+"F3.wireOp",EDGE,"E21.14");var subQ2=makeQuery(id+"F3.imprint","INTERSECT",VERTEX,{"derivedFrom":[subQ1,subQ0]});Q82=makeQuery(id+"F3.imprint","IMPRINT",FACE,{"disambiguationData":[TD([[makeQuery(id+"F3.imprint","IMPRINT",EDGE,{"disambiguationData":[TD([[subQ2,1.0]])],"derivedFrom":subQ1}),-1.0]])]});}
            var Q83;
            {var subQ0=sQuery(id+"F3.wireOp",EDGE,"E41.trimOffspring");var subQ1=sQuery(id+"F3.wireOp",EDGE,"E21.8");var subQ2=makeQuery(id+"F3.imprint","INTERSECT",VERTEX,{"derivedFrom":[subQ1,subQ0]});Q83=makeQuery(id+"F3.imprint","IMPRINT",FACE,{"disambiguationData":[TD([[makeQuery(id+"F3.imprint","IMPRINT",EDGE,{"disambiguationData":[TD([[subQ2,-1.0]])],"derivedFrom":subQ1}),-1.0]])]});}
            var Q84;
            {var subQ5=sQuery(id+"F3.wireOp",EDGE,"E81.trimOffspring");Q84=makeQuery(id+"F3.imprint","IMPRINT",FACE,{"disambiguationData":[TD([[makeQuery(id+"F3.imprint","IMPRINT",EDGE,{"derivedFrom":subQ5}),-1.0]])]});}
            var Q85;
            {var subQ0=sQuery(id+"F3.wireOp",EDGE,"E28.3.0.0");var subQ1=sQuery(id+"F3.wireOp",EDGE,"E21.0");var subQ2=makeQuery(id+"F3.imprint","INTERSECT",VERTEX,{"derivedFrom":[subQ1,subQ0]});Q85=makeQuery(id+"F3.imprint","IMPRINT",FACE,{"disambiguationData":[TD([[makeQuery(id+"F3.imprint","IMPRINT",EDGE,{"disambiguationData":[TD([[subQ2,1.0]])],"derivedFrom":subQ1}),1.0]])]});}
            var Q86;
            {var subQ1=sQuery(id+"F3.wireOp",EDGE,"E21.0");var subQ5=sQuery(id+"F3.wireOp",EDGE,"E25.MirrorCS");var subQ6=makeQuery(id+"F3.imprint","INTERSECT",VERTEX,{"derivedFrom":[subQ1,subQ5]});Q86=makeQuery(id+"F3.imprint","IMPRINT",FACE,{"disambiguationData":[TD([[makeQuery(id+"F3.imprint","IMPRINT",EDGE,{"disambiguationData":[TD([[subQ6,1.0]])],"derivedFrom":subQ1}),1.0]])]});}
            var Q87;
            {var subQ0=sQuery(id+"F3.wireOp",EDGE,"E28.2.0.1");var subQ5=sQuery(id+"F3.wireOp",EDGE,"E21.0");var subQ6=makeQuery(id+"F3.imprint","INTERSECT",VERTEX,{"derivedFrom":[subQ5,subQ0]});Q87=makeQuery(id+"F3.imprint","IMPRINT",FACE,{"disambiguationData":[TD([[makeQuery(id+"F3.imprint","IMPRINT",EDGE,{"disambiguationData":[TD([[subQ6,1.0]])],"derivedFrom":subQ5}),1.0]])]});}
            var Q88;
            {var subQ7=sQuery(id+"F3.wireOp",EDGE,"E21.4");var subQ9=sQuery(id+"F3.wireOp",EDGE,"E73.trimOffspring");var subQ11=makeQuery(id+"F3.imprint","INTERSECT",VERTEX,{"derivedFrom":[subQ7,subQ9]});Q88=makeQuery(id+"F3.imprint","IMPRINT",FACE,{"disambiguationData":[TD([[makeQuery(id+"F3.imprint","IMPRINT",EDGE,{"disambiguationData":[TD([[subQ11,1.0]])],"derivedFrom":subQ7}),-1.0]])]});}
            var Q89;
            {var subQ7=sQuery(id+"F3.wireOp",EDGE,"E68.trimOffspring");var subQ9=sQuery(id+"F3.wireOp",EDGE,"E21.4");var subQ10=makeQuery(id+"F3.imprint","INTERSECT",VERTEX,{"derivedFrom":[subQ9,subQ7]});Q89=makeQuery(id+"F3.imprint","IMPRINT",FACE,{"disambiguationData":[TD([[makeQuery(id+"F3.imprint","IMPRINT",EDGE,{"disambiguationData":[TD([[subQ10,-1.0]])],"derivedFrom":subQ9}),-1.0]])]});}
            extrude(context, id + "F4", {"entities" : qUnion([Q0, Q1, Q2, Q3, Q4, Q5, Q6, Q7, Q8, Q9, Q10, Q11, Q12, Q13, Q14, Q15, Q16, Q17, Q18, Q19, Q20, Q21, Q22, Q23, Q24, Q25, Q26, Q27, Q28, Q29, Q30, Q31, Q32, Q33, Q34, Q35, Q36, Q37, Q38, Q39, Q40, Q41, Q42, Q43, Q44, Q45, Q46, Q47, Q48, Q49, Q50, Q51, Q52, Q53, Q54, Q55, Q56, Q57, Q58, Q59, Q60, Q61, Q62, Q63, Q64, Q65, Q66, Q67, Q68, Q69, Q70, Q71, Q72, Q73, Q74, Q75, Q76, Q77, Q78, Q79, Q80, Q81, Q82, Q83, Q84, Q85, Q86, Q87, Q88, Q89]), "operationType" : NewBodyOperationType.ADD, "depth" : 2 * mm});
        }
        {
            var Q0;
            Q0=makeQuery(id+"F4.opExtrude","SWEPT_EDGE",EDGE,{"disambiguationData":[OSD([sQuery(id+"F3.wireOp",EDGE,"E24"),sQuery(id+"F3.wireOp",EDGE,"E29.0.2.0")])]});
            var Q1;
            Q1=makeQuery(id+"F4.opExtrude","SWEPT_EDGE",EDGE,{"disambiguationData":[OSD([sQuery(id+"F3.wireOp",EDGE,"E25.MirrorCS"),sQuery(id+"F3.wireOp",EDGE,"E31.trimOffspring")])]});
            var Q2;
            Q2=makeQuery(id+"F4.opExtrude","SWEPT_EDGE",EDGE,{"disambiguationData":[OSD([sQuery(id+"F3.wireOp",EDGE,"E28.1.0.0"),sQuery(id+"F3.wireOp",EDGE,"E31.trimOffspring")])]});
            var Q3;
            Q3=makeQuery(id+"F4.opExtrude","SWEPT_EDGE",EDGE,{"disambiguationData":[OSD([sQuery(id+"F3.wireOp",EDGE,"E28.1.0.1"),sQuery(id+"F3.wireOp",EDGE,"E40.trimOffspring")])]});
            var Q4;
            Q4=makeQuery(id+"F4.opExtrude","SWEPT_EDGE",EDGE,{"disambiguationData":[OSD([sQuery(id+"F3.wireOp",EDGE,"E28.2.0.0"),sQuery(id+"F3.wireOp",EDGE,"E40.trimOffspring")])]});
            var Q5;
            Q5=makeQuery(id+"F4.opExtrude","SWEPT_EDGE",EDGE,{"disambiguationData":[OSD([sQuery(id+"F3.wireOp",EDGE,"E28.2.0.1"),sQuery(id+"F3.wireOp",EDGE,"E41.trimOffspring")])]});
            var Q6;
            Q6=makeQuery(id+"F4.opExtrude","SWEPT_EDGE",EDGE,{"disambiguationData":[OSD([sQuery(id+"F3.wireOp",EDGE,"E28.3.0.0"),sQuery(id+"F3.wireOp",EDGE,"E41.trimOffspring")])]});
            var Q7;
            Q7=makeQuery(id+"F4.opExtrude","SWEPT_EDGE",EDGE,{"disambiguationData":[OSD([sQuery(id+"F3.wireOp",EDGE,"E28.3.0.1"),sQuery(id+"F3.wireOp",EDGE,"E42.trimOffspring")])]});
            var Q8;
            Q8=makeQuery(id+"F4.opExtrude","SWEPT_EDGE",EDGE,{"disambiguationData":[OSD([sQuery(id+"F3.wireOp",EDGE,"E39.trimOffspring"),sQuery(id+"F3.wireOp",EDGE,"E58.trimOffspring")])]});
            var Q9;
            Q9=makeQuery(id+"F4.opExtrude","SWEPT_EDGE",EDGE,{"disambiguationData":[OSD([sQuery(id+"F3.wireOp",EDGE,"E38.trimOffspring"),sQuery(id+"F3.wireOp",EDGE,"E57.trimOffspring")])]});
            var Q10;
            Q10=makeQuery(id+"F4.opExtrude","SWEPT_EDGE",EDGE,{"disambiguationData":[OSD([sQuery(id+"F3.wireOp",EDGE,"E37.trimOffspring"),sQuery(id+"F3.wireOp",EDGE,"E57.trimOffspring")])]});
            var Q11;
            Q11=makeQuery(id+"F4.opExtrude","SWEPT_EDGE",EDGE,{"disambiguationData":[OSD([sQuery(id+"F3.wireOp",EDGE,"E36.trimOffspring"),sQuery(id+"F3.wireOp",EDGE,"E56.trimOffspring")])]});
            var Q12;
            Q12=makeQuery(id+"F4.opExtrude","SWEPT_EDGE",EDGE,{"disambiguationData":[OSD([sQuery(id+"F3.wireOp",EDGE,"E34.trimOffspring"),sQuery(id+"F3.wireOp",EDGE,"E46.trimOffspring")])]});
            var Q13;
            Q13=makeQuery(id+"F4.opExtrude","SWEPT_EDGE",EDGE,{"disambiguationData":[OSD([sQuery(id+"F3.wireOp",EDGE,"E35.trimOffspring"),sQuery(id+"F3.wireOp",EDGE,"E56.trimOffspring")])]});
            var Q14;
            Q14=makeQuery(id+"F4.opExtrude","SWEPT_EDGE",EDGE,{"disambiguationData":[OSD([sQuery(id+"F3.wireOp",EDGE,"E29.0.1.0"),sQuery(id+"F3.wireOp",EDGE,"E33.trimOffspring")])]});
            var Q15;
            Q15=makeQuery(id+"F4.opExtrude","SWEPT_EDGE",EDGE,{"disambiguationData":[OSD([sQuery(id+"F3.wireOp",EDGE,"E32.trimOffspring"),sQuery(id+"F3.wireOp",EDGE,"E46.trimOffspring")])]});
            var Q16;
            Q16=makeQuery(id+"F4.opExtrude","SWEPT_EDGE",EDGE,{"disambiguationData":[OSD([sQuery(id+"F3.wireOp",EDGE,"E29.0.1.1"),sQuery(id+"F3.wireOp",EDGE,"E48.trimOffspring")])]});
            var Q17;
            Q17=makeQuery(id+"F4.opExtrude","SWEPT_EDGE",EDGE,{"disambiguationData":[OSD([sQuery(id+"F3.wireOp",EDGE,"E27.MirrorCS"),sQuery(id+"F3.wireOp",EDGE,"E48.trimOffspring")])]});
            var Q18;
            Q18=makeQuery(id+"F4.opExtrude","SWEPT_EDGE",EDGE,{"disambiguationData":[OSD([sQuery(id+"F3.wireOp",EDGE,"E49.trimOffspring"),sQuery(id+"F3.wireOp",EDGE,"E64.trimOffspring")])]});
            var Q19;
            Q19=makeQuery(id+"F4.opExtrude","SWEPT_EDGE",EDGE,{"disambiguationData":[OSD([sQuery(id+"F3.wireOp",EDGE,"E50.trimOffspring"),sQuery(id+"F3.wireOp",EDGE,"E64.trimOffspring")])]});
            var Q20;
            Q20=makeQuery(id+"F4.opExtrude","SWEPT_EDGE",EDGE,{"disambiguationData":[OSD([sQuery(id+"F3.wireOp",EDGE,"E50.trimOffspring"),sQuery(id+"F3.wireOp",EDGE,"E75")])]});
            var Q21;
            Q21=makeQuery(id+"F4.opExtrude","SWEPT_EDGE",EDGE,{"disambiguationData":[OSD([sQuery(id+"F3.wireOp",EDGE,"E51.trimOffspring"),sQuery(id+"F3.wireOp",EDGE,"E63.trimOffspring")])]});
            var Q22;
            Q22=makeQuery(id+"F4.opExtrude","SWEPT_EDGE",EDGE,{"disambiguationData":[OSD([sQuery(id+"F3.wireOp",EDGE,"E52.trimOffspring"),sQuery(id+"F3.wireOp",EDGE,"E63.trimOffspring")])]});
            var Q23;
            Q23=makeQuery(id+"F4.opExtrude","SWEPT_EDGE",EDGE,{"disambiguationData":[OSD([sQuery(id+"F3.wireOp",EDGE,"E52.trimOffspring"),sQuery(id+"F3.wireOp",EDGE,"E59.trimOffspring")])]});
            var Q24;
            Q24=makeQuery(id+"F4.opExtrude","SWEPT_EDGE",EDGE,{"disambiguationData":[OSD([sQuery(id+"F3.wireOp",EDGE,"E53.trimOffspring"),sQuery(id+"F3.wireOp",EDGE,"E62.trimOffspring")])]});
            var Q25;
            Q25=makeQuery(id+"F4.opExtrude","SWEPT_EDGE",EDGE,{"disambiguationData":[OSD([sQuery(id+"F3.wireOp",EDGE,"E54.trimOffspring"),sQuery(id+"F3.wireOp",EDGE,"E62.trimOffspring")])]});
            var Q26;
            Q26=makeQuery(id+"F4.opExtrude","SWEPT_EDGE",EDGE,{"disambiguationData":[OSD([sQuery(id+"F3.wireOp",EDGE,"E55.trimOffspring"),sQuery(id+"F3.wireOp",EDGE,"E61.trimOffspring")])]});
            var Q27;
            Q27=makeQuery(id+"F4.opExtrude","SWEPT_EDGE",EDGE,{"disambiguationData":[OSD([sQuery(id+"F3.wireOp",EDGE,"E54.trimOffspring"),sQuery(id+"F3.wireOp",EDGE,"E78.trimOffspring")])]});
            var Q28;
            Q28=makeQuery(id+"F4.opExtrude","SWEPT_EDGE",EDGE,{"disambiguationData":[OSD([sQuery(id+"F3.wireOp",EDGE,"E68.trimOffspring"),sQuery(id+"F3.wireOp",EDGE,"E80.trimOffspring")])]});
            var Q29;
            Q29=makeQuery(id+"F4.opExtrude","SWEPT_EDGE",EDGE,{"disambiguationData":[OSD([sQuery(id+"F3.wireOp",EDGE,"E26"),sQuery(id+"F3.wireOp",EDGE,"E74.trimOffspring")])]});
            var Q30;
            Q30=makeQuery(id+"F4.opExtrude","SWEPT_EDGE",EDGE,{"disambiguationData":[OSD([sQuery(id+"F3.wireOp",EDGE,"E65.trimOffspring"),sQuery(id+"F3.wireOp",EDGE,"E73.trimOffspring")])]});
            var Q31;
            Q31=makeQuery(id+"F4.opExtrude","SWEPT_EDGE",EDGE,{"disambiguationData":[OSD([sQuery(id+"F3.wireOp",EDGE,"E76"),sQuery(id+"F3.wireOp",EDGE,"E77.trimOffspring")])]});
            var Q32;
            Q32=makeQuery(id+"F4.opExtrude","SWEPT_EDGE",EDGE,{"disambiguationData":[OSD([sQuery(id+"F3.wireOp",EDGE,"E66.trimOffspring"),sQuery(id+"F3.wireOp",EDGE,"E72.trimOffspring")])]});
            var Q33;
            Q33=makeQuery(id+"F4.opExtrude","SWEPT_EDGE",EDGE,{"disambiguationData":[OSD([sQuery(id+"F3.wireOp",EDGE,"E66.trimOffspring"),sQuery(id+"F3.wireOp",EDGE,"E71.trimOffspring")])]});
            var Q34;
            Q34=makeQuery(id+"F4.opExtrude","SWEPT_EDGE",EDGE,{"disambiguationData":[OSD([sQuery(id+"F3.wireOp",EDGE,"E70.trimOffspring"),sQuery(id+"F3.wireOp",EDGE,"E80.trimOffspring")])]});
            var Q35;
            Q35=makeQuery(id+"F4.opExtrude","SWEPT_EDGE",EDGE,{"disambiguationData":[OSD([sQuery(id+"F3.wireOp",EDGE,"E67.trimOffspring"),sQuery(id+"F3.wireOp",EDGE,"E69.trimOffspring")])]});
            var Q36;
            Q36=makeQuery(id+"F4.opExtrude","SWEPT_EDGE",EDGE,{"disambiguationData":[OSD([sQuery(id+"F3.wireOp",EDGE,"E55.trimOffspring"),sQuery(id+"F3.wireOp",EDGE,"E60.trimOffspring")])]});
            var Q37;
            Q37=makeQuery(id+"F4.opExtrude","SWEPT_EDGE",EDGE,{"disambiguationData":[OSD([sQuery(id+"F3.wireOp",EDGE,"E53.trimOffspring"),sQuery(id+"F3.wireOp",EDGE,"E78.trimOffspring")])]});
            var Q38;
            Q38=makeQuery(id+"F4.opExtrude","SWEPT_EDGE",EDGE,{"disambiguationData":[OSD([sQuery(id+"F3.wireOp",EDGE,"E51.trimOffspring"),sQuery(id+"F3.wireOp",EDGE,"E59.trimOffspring")])]});
            var Q39;
            Q39=makeQuery(id+"F4.opExtrude","SWEPT_EDGE",EDGE,{"disambiguationData":[OSD([sQuery(id+"F3.wireOp",EDGE,"E47.trimOffspring"),sQuery(id+"F3.wireOp",EDGE,"E49.trimOffspring")])]});
            var Q40;
            Q40=makeQuery(id+"F4.opExtrude","SWEPT_EDGE",EDGE,{"disambiguationData":[OSD([sQuery(id+"F3.wireOp",EDGE,"E37.trimOffspring"),sQuery(id+"F3.wireOp",EDGE,"E44.trimOffspring")])]});
            var Q41;
            Q41=makeQuery(id+"F4.opExtrude","SWEPT_EDGE",EDGE,{"disambiguationData":[OSD([sQuery(id+"F3.wireOp",EDGE,"E38.trimOffspring"),sQuery(id+"F3.wireOp",EDGE,"E44.trimOffspring")])]});
            var Q42;
            Q42=makeQuery(id+"F4.opExtrude","SWEPT_EDGE",EDGE,{"disambiguationData":[OSD([sQuery(id+"F3.wireOp",EDGE,"E39.trimOffspring"),sQuery(id+"F3.wireOp",EDGE,"E43.trimOffspring")])]});
            var Q43;
            Q43=makeQuery(id+"F4.opExtrude","SWEPT_EDGE",EDGE,{"disambiguationData":[OSD([sQuery(id+"F3.wireOp",EDGE,"E36.trimOffspring"),sQuery(id+"F3.wireOp",EDGE,"E45.trimOffspring")])]});
            var Q44;
            Q44=makeQuery(id+"F4.opExtrude","SWEPT_EDGE",EDGE,{"disambiguationData":[OSD([sQuery(id+"F3.wireOp",EDGE,"E29.0.2.1"),sQuery(id+"F3.wireOp",EDGE,"E33.trimOffspring")])]});
            var Q45;
            Q45=makeQuery(id+"F4.opExtrude","SWEPT_EDGE",EDGE,{"disambiguationData":[OSD([sQuery(id+"F3.wireOp",EDGE,"E30.trimOffspring"),sQuery(id+"F3.wireOp",EDGE,"E32.trimOffspring")])]});
            var Q46;
            Q46=makeQuery(id+"F4.opExtrude","SWEPT_EDGE",EDGE,{"disambiguationData":[OSD([sQuery(id+"F3.wireOp",EDGE,"E30.trimOffspring"),sQuery(id+"F3.wireOp",EDGE,"E34.trimOffspring")])]});
            var Q47;
            Q47=makeQuery(id+"F4.opExtrude","SWEPT_EDGE",EDGE,{"disambiguationData":[OSD([sQuery(id+"F3.wireOp",EDGE,"E35.trimOffspring"),sQuery(id+"F3.wireOp",EDGE,"E45.trimOffspring")])]});
            fillet(context, id + "F5", {"entities" : qUnion([Q0, Q1, Q2, Q3, Q4, Q5, Q6, Q7, Q8, Q9, Q10, Q11, Q12, Q13, Q14, Q15, Q16, Q17, Q18, Q19, Q20, Q21, Q22, Q23, Q24, Q25, Q26, Q27, Q28, Q29, Q30, Q31, Q32, Q33, Q34, Q35, Q36, Q37, Q38, Q39, Q40, Q41, Q42, Q43, Q44, Q45, Q46, Q47]), "radius" : 1 * mm, "tangentPropagation" : true, "conicFillet" : false});
        }
        {
            var Q0;
            Q0=makeQuery(id+"F4.opExtrude","CAP_FACE",FACE,{"disambiguationData":[OSD([sQuery(id+"F0.wireOp",EDGE,"E4.right"),sQuery(id+"F0.wireOp",EDGE,"E7"),sQuery(id+"F0.wireOp",EDGE,"E8.0.1.0"),sQuery(id+"F0.wireOp",EDGE,"E8.2.0.0"),sQuery(id+"F0.wireOp",EDGE,"E8.2.1.0"),sQuery(id+"F0.wireOp",EDGE,"E10.1.0.0"),sQuery(id+"F0.wireOp",EDGE,"E11.MirrorC"),sQuery(id+"F0.wireOp",EDGE,"E13"),sQuery(id+"F0.wireOp",EDGE,"E14"),sQuery(id+"F0.wireOp",EDGE,"E15"),sQuery(id+"F0.wireOp",EDGE,"E16.MirrorC"),sQuery(id+"F0.wireOp",EDGE,"E17.MirrorC"),sQuery(id+"F0.wireOp",EDGE,"E18.MirrorC"),sQuery(id+"F0.wireOp",EDGE,"E19.MirrorC"),sQuery(id+"F0.wireOp",EDGE,"E20.MirrorC"),sQuery(id+"F3.wireOp",EDGE,"E21.0"),sQuery(id+"F3.wireOp",EDGE,"E21.1"),sQuery(id+"F3.wireOp",EDGE,"E21.2"),sQuery(id+"F3.wireOp",EDGE,"E21.3"),sQuery(id+"F3.wireOp",EDGE,"E21.4"),sQuery(id+"F3.wireOp",EDGE,"E21.5"),sQuery(id+"F3.wireOp",EDGE,"E21.6"),sQuery(id+"F3.wireOp",EDGE,"E21.7"),sQuery(id+"F3.wireOp",EDGE,"E21.8"),sQuery(id+"F3.wireOp",EDGE,"E21.9"),sQuery(id+"F3.wireOp",EDGE,"E21.10"),sQuery(id+"F3.wireOp",EDGE,"E21.11"),sQuery(id+"F3.wireOp",EDGE,"E21.12"),sQuery(id+"F3.wireOp",EDGE,"E21.13"),sQuery(id+"F3.wireOp",EDGE,"E21.14"),sQuery(id+"F3.wireOp",EDGE,"E21.15"),sQuery(id+"F3.wireOp",EDGE,"E21.16"),sQuery(id+"F3.wireOp",EDGE,"E21.17"),sQuery(id+"F3.wireOp",EDGE,"E21.18"),sQuery(id+"F3.wireOp",EDGE,"E21.19"),sQuery(id+"F3.wireOp",EDGE,"E22.left"),sQuery(id+"F3.wireOp",EDGE,"E22.right"),sQuery(id+"F3.wireOp",EDGE,"E23.trimOffspring"),sQuery(id+"F3.wireOp",EDGE,"E24"),sQuery(id+"F3.wireOp",EDGE,"E25.MirrorCS"),sQuery(id+"F3.wireOp",EDGE,"E26"),sQuery(id+"F3.wireOp",EDGE,"E27.MirrorCS"),sQuery(id+"F3.wireOp",EDGE,"E28.1.0.0"),sQuery(id+"F3.wireOp",EDGE,"E28.1.0.1"),sQuery(id+"F3.wireOp",EDGE,"E28.2.0.0"),sQuery(id+"F3.wireOp",EDGE,"E28.2.0.1"),sQuery(id+"F3.wireOp",EDGE,"E28.3.0.0"),sQuery(id+"F3.wireOp",EDGE,"E28.3.0.1"),sQuery(id+"F3.wireOp",EDGE,"E29.0.1.0"),sQuery(id+"F3.wireOp",EDGE,"E29.0.1.1"),sQuery(id+"F3.wireOp",EDGE,"E29.0.2.0"),sQuery(id+"F3.wireOp",EDGE,"E29.0.2.1"),sQuery(id+"F3.wireOp",EDGE,"E30.trimOffspring"),sQuery(id+"F3.wireOp",EDGE,"E31.trimOffspring"),sQuery(id+"F3.wireOp",EDGE,"E32.trimOffspring"),sQuery(id+"F3.wireOp",EDGE,"E33.trimOffspring"),sQuery(id+"F3.wireOp",EDGE,"E34.trimOffspring"),sQuery(id+"F3.wireOp",EDGE,"E37.trimOffspring"),sQuery(id+"F3.wireOp",EDGE,"E38.trimOffspring"),sQuery(id+"F3.wireOp",EDGE,"E39.trimOffspring"),sQuery(id+"F3.wireOp",EDGE,"E40.trimOffspring"),sQuery(id+"F3.wireOp",EDGE,"E41.trimOffspring"),sQuery(id+"F3.wireOp",EDGE,"E42.trimOffspring"),sQuery(id+"F3.wireOp",EDGE,"E43.trimOffspring"),sQuery(id+"F3.wireOp",EDGE,"E44.trimOffspring"),sQuery(id+"F3.wireOp",EDGE,"E46.trimOffspring"),sQuery(id+"F3.wireOp",EDGE,"E47.trimOffspring"),sQuery(id+"F3.wireOp",EDGE,"E48.trimOffspring"),sQuery(id+"F3.wireOp",EDGE,"E49.trimOffspring"),sQuery(id+"F3.wireOp",EDGE,"E50.trimOffspring"),sQuery(id+"F3.wireOp",EDGE,"E53.trimOffspring"),sQuery(id+"F3.wireOp",EDGE,"E54.trimOffspring"),sQuery(id+"F3.wireOp",EDGE,"E55.trimOffspring"),sQuery(id+"F3.wireOp",EDGE,"E57.trimOffspring"),sQuery(id+"F3.wireOp",EDGE,"E58.trimOffspring"),sQuery(id+"F3.wireOp",EDGE,"E60.trimOffspring"),sQuery(id+"F3.wireOp",EDGE,"E61.trimOffspring"),sQuery(id+"F3.wireOp",EDGE,"E62.trimOffspring"),sQuery(id+"F3.wireOp",EDGE,"E64.trimOffspring"),sQuery(id+"F3.wireOp",EDGE,"E65.trimOffspring"),sQuery(id+"F3.wireOp",EDGE,"E66.trimOffspring"),sQuery(id+"F3.wireOp",EDGE,"E67.trimOffspring"),sQuery(id+"F3.wireOp",EDGE,"E68.trimOffspring"),sQuery(id+"F3.wireOp",EDGE,"E69.trimOffspring"),sQuery(id+"F3.wireOp",EDGE,"E70.trimOffspring"),sQuery(id+"F3.wireOp",EDGE,"E71.trimOffspring"),sQuery(id+"F3.wireOp",EDGE,"E72.trimOffspring"),sQuery(id+"F3.wireOp",EDGE,"E73.trimOffspring"),sQuery(id+"F3.wireOp",EDGE,"E74.trimOffspring"),sQuery(id+"F3.wireOp",EDGE,"E75"),sQuery(id+"F3.wireOp",EDGE,"E76"),sQuery(id+"F3.wireOp",EDGE,"E77.trimOffspring"),sQuery(id+"F3.wireOp",EDGE,"E78.trimOffspring"),sQuery(id+"F3.wireOp",EDGE,"E80.trimOffspring"),sQuery(id+"F3.wireOp",EDGE,"E81.trimOffspring"),sQuery(id+"F3.wireOp",EDGE,"E82.trimOffspring")])],"isStart":false});
            var sketch = newSketch(context, id + "F6", { "sketchPlane" : qUnion([Q0]) });
            skLineSegment(sketch, "E84.0", {"start": v(9.9, 0) * mm, "end": v(9.9, -11.4) * mm, "construction": true});
            skLineSegment(sketch, "E84.1", {"start": v(70.8, -11.4) * mm, "end": v(-11.4, -11.4) * mm, "construction": true});
            skLineSegment(sketch, "E85.bottom", {"start": v(11.4, -10.15) * mm, "end": v(8.4, -10.15) * mm});
            skLineSegment(sketch, "E85.top", {"start": v(11.4, -9.05) * mm, "end": v(8.4, -9.05) * mm});
            skLineSegment(sketch, "E85.left", {"start": v(11.4, -10.15) * mm, "end": v(11.4, -9.05) * mm});
            skLineSegment(sketch, "E85.right", {"start": v(8.4, -10.15) * mm, "end": v(8.4, -9.05) * mm});
            skPoint(sketch, "E85.middle", {"position": v(9.9, -9.6) * mm});
            skLineSegment(sketch, "E86.bottom", {"start": v(11.4, -6.7) * mm, "end": v(8.4, -6.7) * mm});
            skLineSegment(sketch, "E86.top", {"start": v(11.4, -7.8) * mm, "end": v(8.4, -7.8) * mm});
            skLineSegment(sketch, "E86.left", {"start": v(11.4, -6.7) * mm, "end": v(11.4, -7.8) * mm});
            skLineSegment(sketch, "E86.right", {"start": v(8.4, -6.7) * mm, "end": v(8.4, -7.8) * mm});
            skPoint(sketch, "E86.middle", {"position": v(9.9, -7.25) * mm});
            skLineSegment(sketch, "E87.MirrorCS", {"start": v(11.4, 46.3) * mm, "end": v(8.4, 46.3) * mm});
            skLineSegment(sketch, "E88.MirrorCS", {"start": v(8.4, 46.3) * mm, "end": v(8.4, 47.4) * mm});
            skLineSegment(sketch, "E89.MirrorCS", {"start": v(11.4, 47.4) * mm, "end": v(8.4, 47.4) * mm});
            skLineSegment(sketch, "E90.MirrorCS", {"start": v(11.4, 46.3) * mm, "end": v(11.4, 47.4) * mm});
            skLineSegment(sketch, "E91.MirrorCS", {"start": v(11.4, 48.65) * mm, "end": v(8.4, 48.65) * mm});
            skLineSegment(sketch, "E92.MirrorCS", {"start": v(8.4, 49.75) * mm, "end": v(8.4, 48.65) * mm});
            skLineSegment(sketch, "E93.MirrorCS", {"start": v(11.4, 49.75) * mm, "end": v(8.4, 49.75) * mm});
            skLineSegment(sketch, "E94.MirrorCS", {"start": v(11.4, 49.75) * mm, "end": v(11.4, 48.65) * mm});
            skLineSegment(sketch, "E95.MirrorCS", {"start": v(48, 49.75) * mm, "end": v(51, 49.75) * mm});
            skLineSegment(sketch, "E96.MirrorCS", {"start": v(51, 49.75) * mm, "end": v(51, 48.65) * mm});
            skLineSegment(sketch, "E97.MirrorCS", {"start": v(48, 48.65) * mm, "end": v(51, 48.65) * mm});
            skLineSegment(sketch, "E98.MirrorCS", {"start": v(48, 49.75) * mm, "end": v(48, 48.65) * mm});
            skLineSegment(sketch, "E99.MirrorCS", {"start": v(51, 46.3) * mm, "end": v(51, 47.4) * mm});
            skLineSegment(sketch, "E100.MirrorCS", {"start": v(48, 47.4) * mm, "end": v(51, 47.4) * mm});
            skLineSegment(sketch, "E101.MirrorCS", {"start": v(48, 46.3) * mm, "end": v(48, 47.4) * mm});
            skLineSegment(sketch, "E102.MirrorCS", {"start": v(48, 46.3) * mm, "end": v(51, 46.3) * mm});
            skLineSegment(sketch, "E103.MirrorCS", {"start": v(48, -6.7) * mm, "end": v(51, -6.7) * mm});
            skLineSegment(sketch, "E104.MirrorCS", {"start": v(51, -6.7) * mm, "end": v(51, -7.8) * mm});
            skLineSegment(sketch, "E105.MirrorCS", {"start": v(48, -7.8) * mm, "end": v(51, -7.8) * mm});
            skLineSegment(sketch, "E106.MirrorCS", {"start": v(48, -6.7) * mm, "end": v(48, -7.8) * mm});
            skLineSegment(sketch, "E107.MirrorCS", {"start": v(48, -9.05) * mm, "end": v(51, -9.05) * mm});
            skLineSegment(sketch, "E108.MirrorCS", {"start": v(51, -10.15) * mm, "end": v(51, -9.05) * mm});
            skLineSegment(sketch, "E109.MirrorCS", {"start": v(48, -10.15) * mm, "end": v(51, -10.15) * mm});
            skLineSegment(sketch, "E110.MirrorCS", {"start": v(48, -10.15) * mm, "end": v(48, -9.05) * mm});
            skSolve(sketch);
        }
        {
            var Q0;
            Q0 = qSketchRegion(id + "F6", true);
            extrude(context, id + "F7", {"entities" : qUnion([Q0]), "operationType" : NewBodyOperationType.REMOVE, "endBound" : BoundingType.THROUGH_ALL, "oppositeDirection" : true, "depth" : 25 * mm});
        }
    });
